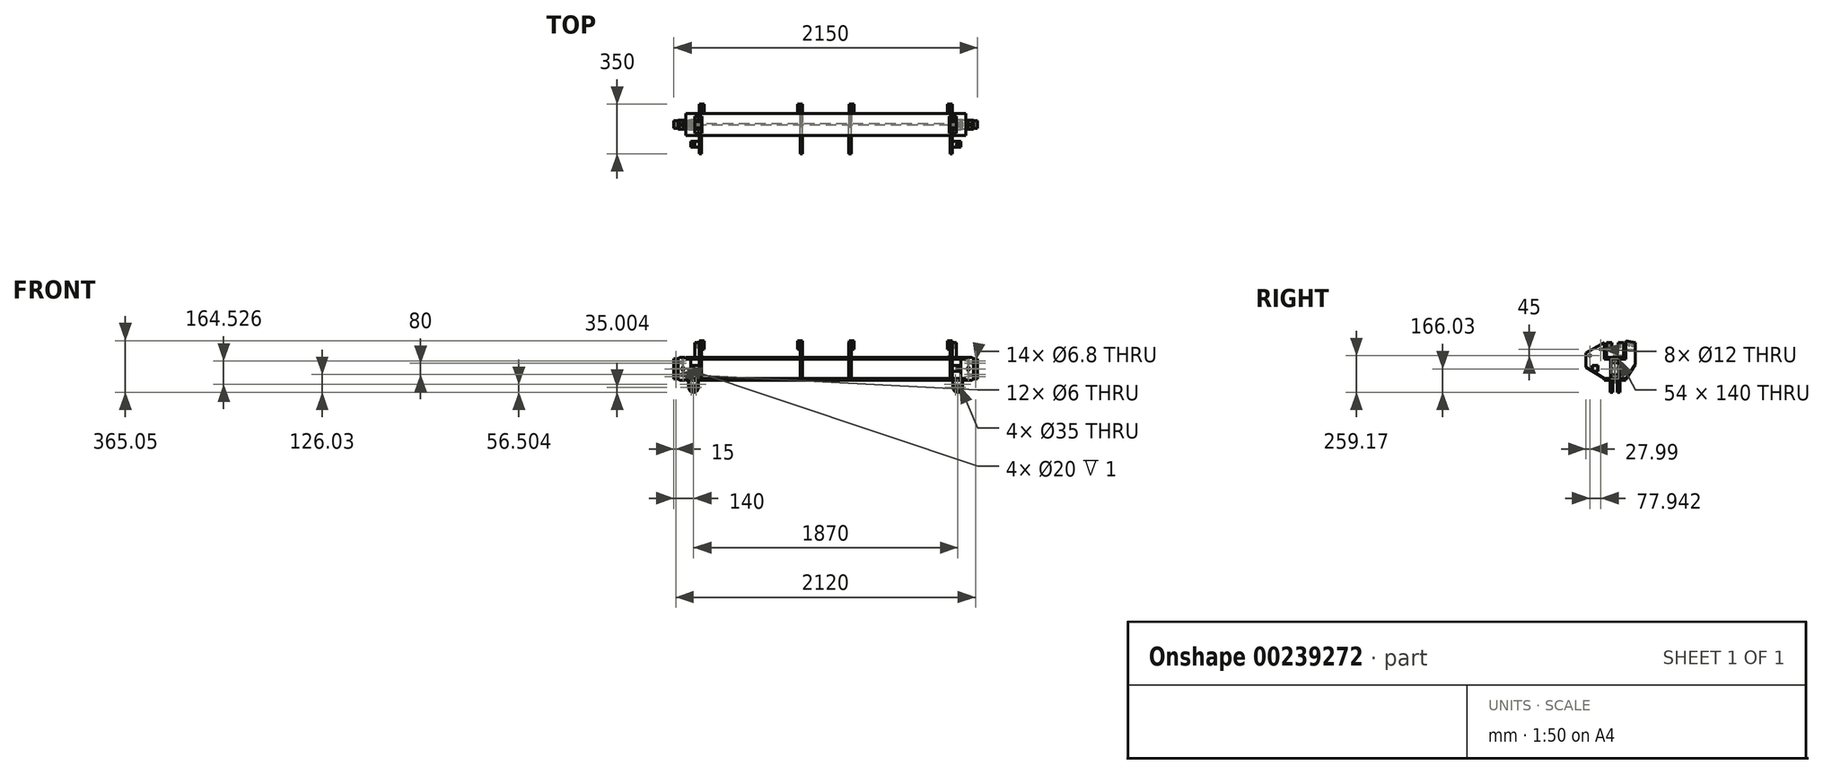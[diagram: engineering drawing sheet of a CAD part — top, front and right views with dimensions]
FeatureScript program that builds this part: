
annotation { "Feature Type Name" : "Feature", "Feature Type Description" : "" }
export const myFeature = defineFeature(function(context is Context, id is Id, definition is map)
    precondition{}
    {
        {
            var Q0;
            Q0=qCreatedBy(makeId("Right.planeOp"),FACE);
            var sketch = newSketch(context, id + "F0", { "sketchPlane" : qUnion([Q0])});
            skLineSegment(sketch, "E0.bottom", {"start": v(-77.22, 81.03) * mm, "end": v(77.22, 81.03) * mm});
            skLineSegment(sketch, "E0.top", {"start": v(-77.22, -81.03) * mm, "end": v(77.22, -81.03) * mm});
            skLineSegment(sketch, "E0.left", {"start": v(-77.22, 81.03) * mm, "end": v(-77.22, 69.47) * mm});
            skLineSegment(sketch, "E0.right", {"start": v(77.22, 81.03) * mm, "end": v(77.22, 69.47) * mm});
            skPoint(sketch, "E0.middle", {"position": v(0, 0) * mm});
            skLineSegment(sketch, "E1", {"start": v(0, 87.3) * mm, "end": v(0, -92.44) * mm, "construction": true});
            skLineSegment(sketch, "E2.0", {"start": v(-77.22, 69.47) * mm, "end": v(-16.76, 69.47) * mm});
            skLineSegment(sketch, "E3.0", {"start": v(-77.22, -69.47) * mm, "end": v(-16.76, -69.47) * mm});
            skLineSegment(sketch, "E4.0", {"start": v(-4.06, 56.77) * mm, "end": v(-4.06, -56.77) * mm});
            skLineSegment(sketch, "E5.0", {"start": v(4.06, 56.77) * mm, "end": v(4.06, -56.77) * mm});
            skLineSegment(sketch, "E6.trimOffspring", {"start": v(16.76, -69.47) * mm, "end": v(77.22, -69.47) * mm});
            skLineSegment(sketch, "E7.trimOffspring", {"start": v(16.76, 69.47) * mm, "end": v(77.22, 69.47) * mm});
            skLineSegment(sketch, "E8.trimOffspring", {"start": v(-77.22, -69.47) * mm, "end": v(-77.22, -81.03) * mm});
            skLineSegment(sketch, "E9.trimOffspring", {"start": v(77.22, -69.47) * mm, "end": v(77.22, -81.03) * mm});
            skPoint(sketch, "E10.visualSharp", {"position": v(-4.06, 69.47) * mm});
            skArc(sketch, "E10.filletArc", {"start": v(-4.06, 56.77) * mm, "mid": v(-7.78, 65.75) * mm, "end": v(-16.76, 69.47) * mm});
            skPoint(sketch, "E11.visualSharp", {"position": v(4.06, 69.47) * mm});
            skArc(sketch, "E11.filletArc", {"start": v(16.76, 69.47) * mm, "mid": v(7.78, 65.75) * mm, "end": v(4.06, 56.77) * mm});
            skPoint(sketch, "E12.visualSharp", {"position": v(4.06, -69.47) * mm});
            skArc(sketch, "E12.filletArc", {"start": v(4.06, -56.77) * mm, "mid": v(7.78, -65.75) * mm, "end": v(16.76, -69.47) * mm});
            skPoint(sketch, "E13.visualSharp", {"position": v(-4.06, -69.47) * mm});
            skArc(sketch, "E13.filletArc", {"start": v(-16.76, -69.47) * mm, "mid": v(-7.78, -65.75) * mm, "end": v(-4.06, -56.77) * mm});
            skSolve(sketch);
        }
        {
            var Q0;
            Q0 = qSketchRegion(id + "F0", true);
            extrude(context, id + "F1", {"entities" : qUnion([Q0]), "endBound" : BoundingType.SYMMETRIC, "depth" : 1980 * mm});
        }
        {
            var Q0;
            Q0=makeQuery(id+"F1.opExtrude","SWEPT_FACE",FACE,{"disambiguationData":[OSD([sQuery(id+"F0.wireOp",EDGE,"E4.0")])]});
            var sketch = newSketch(context, id + "F2", { "sketchPlane" : qUnion([Q0])});
            skLineSegment(sketch, "E14", {"start": v(0, 173.84) * mm, "end": v(0, -192.2) * mm, "construction": true});
            skLineSegment(sketch, "E15.0", {"start": v(-990, 69.47) * mm, "end": v(-990, -69.47) * mm, "construction": true});
            skLineSegment(sketch, "E16.0", {"start": v(990, 69.47) * mm, "end": v(-990, 69.47) * mm, "construction": true});
            skLineSegment(sketch, "E17.0", {"start": v(990, -69.47) * mm, "end": v(-990, -69.47) * mm, "construction": true});
            skPoint(sketch, "E18.orphan", {"position": v(-990, 56.77) * mm});
            skPoint(sketch, "E19.orphan", {"position": v(-990, -56.77) * mm});
            skLineSegment(sketch, "E20.bottom", {"start": v(-990, 69.47) * mm, "end": v(-955, 69.47) * mm});
            skLineSegment(sketch, "E20.top", {"start": v(-990, -69.47) * mm, "end": v(-955, -69.47) * mm});
            skLineSegment(sketch, "E20.left", {"start": v(-990, 69.47) * mm, "end": v(-990, -69.47) * mm});
            skLineSegment(sketch, "E20.right", {"start": v(-955, 69.47) * mm, "end": v(-955, -69.47) * mm});
            skLineSegment(sketch, "E21.MirrorCS", {"start": v(990, -69.47) * mm, "end": v(955, -69.47) * mm});
            skLineSegment(sketch, "E22.MirrorCS", {"start": v(990, 69.47) * mm, "end": v(955, 69.47) * mm});
            skLineSegment(sketch, "E23.MirrorCS", {"start": v(990, 69.47) * mm, "end": v(990, -69.47) * mm});
            skLineSegment(sketch, "E24.MirrorCS", {"start": v(955, 69.47) * mm, "end": v(955, -69.47) * mm});
            skPoint(sketch, "E25.MirrorP", {"position": v(990, -56.77) * mm});
            skPoint(sketch, "E26.MirrorP", {"position": v(990, 56.77) * mm});
            skLineSegment(sketch, "E27.MirrorCS", {"start": v(990, 69.47) * mm, "end": v(990, -69.47) * mm, "construction": true});
            skSolve(sketch);
        }
        {
            var Q0;
            Q0 = qSketchRegion(id + "F2", true);
            extrude(context, id + "F3", {"entities" : qUnion([Q0]), "operationType" : NewBodyOperationType.REMOVE, "endBound" : BoundingType.SYMMETRIC, "oppositeDirection" : true, "depth" : 50 * mm});
        }
        {
            var Q0;
            Q0=qCreatedBy(makeId("Front.planeOp"),FACE);
            var sketch = newSketch(context, id + "F4", { "sketchPlane" : qUnion([Q0])});
            skLineSegment(sketch, "E28", {"start": v(0, 276.7) * mm, "end": v(0, -349.05) * mm, "construction": true});
            skLineSegment(sketch, "E29.0", {"start": v(-1075, 276.7) * mm, "end": v(-1075, -349.05) * mm, "construction": true});
            skLineSegment(sketch, "E30.0", {"start": v(990, 81.03) * mm, "end": v(-1045, 81.03) * mm, "construction": true});
            skLineSegment(sketch, "E31.0", {"start": v(990, -81.03) * mm, "end": v(-1045, -81.03) * mm, "construction": true});
            skLineSegment(sketch, "E32.0", {"start": v(-955, -69.47) * mm, "end": v(-955, 69.47) * mm, "construction": true});
            skLineSegment(sketch, "E33.0", {"start": v(990, -69.47) * mm, "end": v(-990, -69.47) * mm, "construction": true});
            skLineSegment(sketch, "E34.0", {"start": v(990, 69.47) * mm, "end": v(-990, 69.47) * mm, "construction": true});
            skPoint(sketch, "E35.orphan", {"position": v(-955, 56.77) * mm});
            skPoint(sketch, "E36.orphan", {"position": v(-955, -56.77) * mm});
            skPoint(sketch, "E37.orphan", {"position": v(-990, 81.03) * mm});
            skPoint(sketch, "E38.orphan", {"position": v(-990, -81.03) * mm});
            skLineSegment(sketch, "E39", {"start": v(-990, 81.03) * mm, "end": v(-990, 69.47) * mm, "construction": true});
            skLineSegment(sketch, "E40.0", {"start": v(-1045, 81.03) * mm, "end": v(-1045, 70) * mm, "construction": true});
            skLineSegment(sketch, "E41", {"start": v(0, 0) * mm, "end": v(-1199.42, 0) * mm, "construction": true});
            skLineSegment(sketch, "E42.0", {"start": v(0, 70) * mm, "end": v(-990, 70) * mm, "construction": true});
            skLineSegment(sketch, "E43.trimOffspring", {"start": v(-1045, 70) * mm, "end": v(-1075, 70) * mm, "construction": true});
            skLineSegment(sketch, "E44.MirrorCS", {"start": v(-1045, -70) * mm, "end": v(-1075, -70) * mm, "construction": true});
            skPoint(sketch, "E45.orphan", {"position": v(-1199.42, 70) * mm});
            skPoint(sketch, "E46.orphan", {"position": v(-1199.42, -70) * mm});
            skLineSegment(sketch, "E47.trimOffspring", {"start": v(-1045, -70) * mm, "end": v(-1045, -81.03) * mm, "construction": true});
            skLineSegment(sketch, "E48.trimOffspring", {"start": v(-990, -69.47) * mm, "end": v(-990, -81.03) * mm, "construction": true});
            skLineSegment(sketch, "E49.bottom", {"start": v(-1075, 70) * mm, "end": v(-1045, 70) * mm});
            skLineSegment(sketch, "E49.top", {"start": v(-1075, -70) * mm, "end": v(-1045, -70) * mm});
            skLineSegment(sketch, "E49.left", {"start": v(-1075, 70) * mm, "end": v(-1075, -70) * mm});
            skLineSegment(sketch, "E50.bottom", {"start": v(-1045, 81.03) * mm, "end": v(-990, 81.03) * mm});
            skLineSegment(sketch, "E50.top", {"start": v(-1045, -81.03) * mm, "end": v(-990, -81.03) * mm});
            skLineSegment(sketch, "E50.left", {"start": v(-1045, 81.03) * mm, "end": v(-1045, 70) * mm});
            skLineSegment(sketch, "E50.right", {"start": v(-990, 81.03) * mm, "end": v(-990, 69.47) * mm});
            skLineSegment(sketch, "E51.bottom", {"start": v(-990, 70) * mm, "end": v(-955, 70) * mm});
            skLineSegment(sketch, "E51.top", {"start": v(-990, -69.47) * mm, "end": v(-955, -69.47) * mm});
            skLineSegment(sketch, "E51.left", {"start": v(-990, 70) * mm, "end": v(-990, 69.47) * mm});
            skLineSegment(sketch, "E51.right", {"start": v(-955, 70) * mm, "end": v(-955, -69.47) * mm});
            skLineSegment(sketch, "E52.trimOffspring", {"start": v(-990, -69.47) * mm, "end": v(-990, -81.03) * mm});
            skLineSegment(sketch, "E53.trimOffspring", {"start": v(-1045, -70) * mm, "end": v(-1045, -81.03) * mm});
            skSolve(sketch);
        }
        {
            var Q0;
            Q0 = qSketchRegion(id + "F4", true);
            extrude(context, id + "F5", {"entities" : qUnion([Q0]), "endBound" : BoundingType.SYMMETRIC, "depth" : 63.5 * mm});
        }
        {
            var Q0;
            Q0=makeQuery(id+"F5.opExtrude","SWEPT_FACE",FACE,{"disambiguationData":[OSD([sQuery(id+"F4.wireOp",EDGE,"E49.bottom")])]});
            var sketch = newSketch(context, id + "F6", { "sketchPlane" : qUnion([Q0])});
            skLineSegment(sketch, "E54", {"start": v(-948.4, 0) * mm, "end": v(-1101.52, 0) * mm, "construction": true});
            skLineSegment(sketch, "E55.0", {"start": v(-1045, -31.75) * mm, "end": v(-1045, 31.75) * mm, "construction": true});
            skLineSegment(sketch, "E56.0", {"start": v(-948.4, 27) * mm, "end": v(-1101.52, 27) * mm, "construction": true});
            skLineSegment(sketch, "E57.bottom", {"start": v(-1075, 31.75) * mm, "end": v(-1045, 31.75) * mm});
            skLineSegment(sketch, "E57.top", {"start": v(-1075, 27) * mm, "end": v(-1045, 27) * mm});
            skLineSegment(sketch, "E57.left", {"start": v(-1075, 31.75) * mm, "end": v(-1075, 27) * mm});
            skLineSegment(sketch, "E57.right", {"start": v(-1045, 31.75) * mm, "end": v(-1045, 27) * mm});
            skLineSegment(sketch, "E58.MirrorCS", {"start": v(-1045, -31.75) * mm, "end": v(-1045, -27) * mm});
            skLineSegment(sketch, "E59.MirrorCS", {"start": v(-1075, -31.75) * mm, "end": v(-1075, -27) * mm});
            skLineSegment(sketch, "E60.MirrorCS", {"start": v(-1075, -27) * mm, "end": v(-1045, -27) * mm});
            skLineSegment(sketch, "E61.MirrorCS", {"start": v(-1075, -31.75) * mm, "end": v(-1045, -31.75) * mm});
            skSolve(sketch);
        }
        {
            var Q0;
            Q0 = qSketchRegion(id + "F6", true);
            extrude(context, id + "F7", {"entities" : qUnion([Q0]), "operationType" : NewBodyOperationType.REMOVE, "endBound" : BoundingType.THROUGH_ALL, "oppositeDirection" : true, "depth" : 25 * mm});
        }
        {
            var Q0;
            Q0=makeQuery(id+"F5.opExtrude","SWEPT_FACE",FACE,{"disambiguationData":[OSD([sQuery(id+"F4.wireOp",EDGE,"E50.bottom")])]});
            var sketch = newSketch(context, id + "F8", { "sketchPlane" : qUnion([Q0])});
            skLineSegment(sketch, "E62.0", {"start": v(-1075, -27) * mm, "end": v(-1075, 27) * mm, "construction": true});
            skLineSegment(sketch, "E63", {"start": v(-919.6, 0) * mm, "end": v(-1088.25, 0) * mm, "construction": true});
            skPoint(sketch, "E63.endSnap0", {"position": v(-1075, 0) * mm});
            skLineSegment(sketch, "E64.0", {"start": v(-1010, -27) * mm, "end": v(-1010, 27) * mm, "construction": true});
            skPoint(sketch, "E65", {"position": v(-1010, 0) * mm});
            skSolve(sketch);
        }
        {
            var Q0;
            Q0=sQuery(id+"F8.wireOp",VERTEX,"E65");
            var Q1;
            Q1=makeQuery(id+"F5.opExtrude","SWEPT_BODY",BODY,{"disambiguationData":[OSD([sQuery(id+"F4.wireOp",EDGE,"E49.bottom"),sQuery(id+"F4.wireOp",EDGE,"E49.top"),sQuery(id+"F4.wireOp",EDGE,"E49.left"),sQuery(id+"F4.wireOp",EDGE,"E50.bottom"),sQuery(id+"F4.wireOp",EDGE,"E50.top"),sQuery(id+"F4.wireOp",EDGE,"E50.left"),sQuery(id+"F4.wireOp",EDGE,"E50.right"),sQuery(id+"F4.wireOp",EDGE,"E51.bottom"),sQuery(id+"F4.wireOp",EDGE,"E51.top"),sQuery(id+"F4.wireOp",EDGE,"E51.right"),sQuery(id+"F4.wireOp",EDGE,"E52.trimOffspring"),sQuery(id+"F4.wireOp",EDGE,"E53.trimOffspring")])]});
            hole(context, id + "F9", {"style" : HoleStyle.SIMPLE, "endStyle" : HoleEndStyle.BLIND, "standardTappedOrClearance" : lookupTablePath({ "standard" : "ISO", "size" : "6", "type" : "Drilled" }), "standardBlindInLast" : lookupTablePath({ "standard" : "ISO", "size" : "6", "type" : "Drilled" }), "holeDiameter" : 6 * mm, "holeDepth" : 125 * mm, "locations" : qUnion([Q0]), "scope" : qUnion([Q1])});
        }
        {
            var Q0;
            Q0=sQuery(id+"F8.wireOp",VERTEX,"E65");
            var Q1;
            Q1=makeQuery(id+"F5.opExtrude","SWEPT_BODY",BODY,{"disambiguationData":[OSD([sQuery(id+"F4.wireOp",EDGE,"E49.bottom"),sQuery(id+"F4.wireOp",EDGE,"E49.top"),sQuery(id+"F4.wireOp",EDGE,"E49.left"),sQuery(id+"F4.wireOp",EDGE,"E50.bottom"),sQuery(id+"F4.wireOp",EDGE,"E50.top"),sQuery(id+"F4.wireOp",EDGE,"E50.left"),sQuery(id+"F4.wireOp",EDGE,"E50.right"),sQuery(id+"F4.wireOp",EDGE,"E51.bottom"),sQuery(id+"F4.wireOp",EDGE,"E51.top"),sQuery(id+"F4.wireOp",EDGE,"E51.right"),sQuery(id+"F4.wireOp",EDGE,"E52.trimOffspring"),sQuery(id+"F4.wireOp",EDGE,"E53.trimOffspring")])]});
            hole(context, id + "F10", {"style" : HoleStyle.SIMPLE, "endStyle" : HoleEndStyle.BLIND, "standardTappedOrClearance" : lookupTablePath({ "standard" : "ANSI", "engagement" : "75%", "pitch" : "13 tpi", "size" : "1/2", "type" : "Tapped" }), "standardBlindInLast" : lookupTablePath({ "standard" : "ANSI", "engagement" : "75%", "pitch" : "13 tpi", "size" : "1/2", "type" : "Tapped" }), "holeDiameter" : 10.72 * mm, "holeDepth" : 15 * mm, "locations" : qUnion([Q0]), "scope" : qUnion([Q1]), "majorDiameter" : 12.7 * mm});
        }
        {
            var Q0;
            {var subQ0=sQuery(id+"F4.wireOp",EDGE,"E50.bottom");Q0=makeQuery(id+"F8.imprint","IMPRINT",FACE,{"disambiguationData":[TD([[makeQuery(id+"F8.imprint","IMPRINT",EDGE,{"derivedFrom":makeQuery(id+"F5.opExtrude","CAP_EDGE",EDGE,{"disambiguationData":[OSD([subQ0])],"isStart":true})}),-1.0]])]});}
            var sketch = newSketch(context, id + "F11", { "sketchPlane" : qUnion([Q0])});
            skPoint(sketch, "E66.0", {"position": v(-1010, 0) * mm});
            skCircle(sketch, "E67", {"center": v(-1010, 0) * mm, "radius": 10 * mm});
            skSolve(sketch);
        }
        {
            var Q0;
            Q0 = qSketchRegion(id + "F11", true);
            extrude(context, id + "F12", {"entities" : qUnion([Q0]), "operationType" : NewBodyOperationType.REMOVE, "oppositeDirection" : true, "depth" : 1 * mm});
        }
        {
            var Q0;
            Q0=makeQuery(id+"F5.opExtrude","SWEPT_EDGE",EDGE,{"disambiguationData":[OSD([sQuery(id+"F4.wireOp",EDGE,"E50.bottom"),sQuery(id+"F4.wireOp",EDGE,"E50.left")])]});
            var Q1;
            Q1=makeQuery(id+"F7.boolean.opBoolean","INTERSECT",EDGE,{"derivedFrom":[makeQuery(id+"F7.opExtrude","SWEPT_FACE",FACE,{"disambiguationData":[OSD([sQuery(id+"F6.wireOp",EDGE,"E57.right")])]}),makeQuery(id+"F7.opExtrude","SWEPT_FACE",FACE,{"disambiguationData":[OSD([sQuery(id+"F6.wireOp",EDGE,"E58.MirrorCS")])]})]});
            chamfer(context, id + "F13", {"entities" : qUnion([Q0, Q1]), "width" : 11 * mm, "tangentPropagation" : true});
        }
        {
            var Q0;
            Q0=makeQuery(id+"F5.opExtrude","CAP_FACE",FACE,{"disambiguationData":[OSD([sQuery(id+"F4.wireOp",EDGE,"E49.bottom"),sQuery(id+"F4.wireOp",EDGE,"E49.top"),sQuery(id+"F4.wireOp",EDGE,"E49.left"),sQuery(id+"F4.wireOp",EDGE,"E50.bottom"),sQuery(id+"F4.wireOp",EDGE,"E50.top"),sQuery(id+"F4.wireOp",EDGE,"E50.left"),sQuery(id+"F4.wireOp",EDGE,"E50.right"),sQuery(id+"F4.wireOp",EDGE,"E51.bottom"),sQuery(id+"F4.wireOp",EDGE,"E51.top"),sQuery(id+"F4.wireOp",EDGE,"E51.right"),sQuery(id+"F4.wireOp",EDGE,"E52.trimOffspring"),sQuery(id+"F4.wireOp",EDGE,"E53.trimOffspring")])],"isStart":false});
            var sketch = newSketch(context, id + "F14", { "sketchPlane" : qUnion([Q0])});
            skLineSegment(sketch, "E68", {"start": v(-947.26, 0.27) * mm, "end": v(-1104.17, 0.27) * mm, "construction": true});
            skPoint(sketch, "E68.startSnap0", {"position": v(-955, 0.27) * mm});
            skLineSegment(sketch, "E69.0", {"start": v(-1075, -70) * mm, "end": v(-1075, 70) * mm, "construction": true});
            skLineSegment(sketch, "E70.0", {"start": v(-1010, -70) * mm, "end": v(-1010, 70) * mm, "construction": true});
            skPoint(sketch, "E71", {"position": v(-1010, 0.27) * mm});
            skSolve(sketch);
        }
        {
            var Q0;
            Q0=sQuery(id+"F14.wireOp",VERTEX,"E71");
            var Q1;
            Q1=makeQuery(id+"F5.opExtrude","SWEPT_BODY",BODY,{"disambiguationData":[OSD([sQuery(id+"F4.wireOp",EDGE,"E49.bottom"),sQuery(id+"F4.wireOp",EDGE,"E49.top"),sQuery(id+"F4.wireOp",EDGE,"E49.left"),sQuery(id+"F4.wireOp",EDGE,"E50.bottom"),sQuery(id+"F4.wireOp",EDGE,"E50.top"),sQuery(id+"F4.wireOp",EDGE,"E50.left"),sQuery(id+"F4.wireOp",EDGE,"E50.right"),sQuery(id+"F4.wireOp",EDGE,"E51.bottom"),sQuery(id+"F4.wireOp",EDGE,"E51.top"),sQuery(id+"F4.wireOp",EDGE,"E51.right"),sQuery(id+"F4.wireOp",EDGE,"E52.trimOffspring"),sQuery(id+"F4.wireOp",EDGE,"E53.trimOffspring")])]});
            hole(context, id + "F15", {"style" : HoleStyle.SIMPLE, "endStyle" : HoleEndStyle.BLIND, "standardTappedOrClearance" : lookupTablePath({ "standard" : "ANSI", "engagement" : "75%", "pitch" : "13 tpi", "size" : "1/2", "type" : "Tapped" }), "standardBlindInLast" : lookupTablePath({ "standard" : "ANSI", "engagement" : "75%", "pitch" : "13 tpi", "size" : "1/2", "type" : "Tapped" }), "holeDiameter" : 10.72 * mm, "holeDepth" : 15 * mm, "locations" : qUnion([Q0]), "scope" : qUnion([Q1]), "majorDiameter" : 12.7 * mm});
        }
        {
            var Q0;
            Q0=sQuery(id+"F14.wireOp",VERTEX,"E71");
            var Q1;
            Q1=makeQuery(id+"F5.opExtrude","SWEPT_BODY",BODY,{"disambiguationData":[OSD([sQuery(id+"F4.wireOp",EDGE,"E49.bottom"),sQuery(id+"F4.wireOp",EDGE,"E49.top"),sQuery(id+"F4.wireOp",EDGE,"E49.left"),sQuery(id+"F4.wireOp",EDGE,"E50.bottom"),sQuery(id+"F4.wireOp",EDGE,"E50.top"),sQuery(id+"F4.wireOp",EDGE,"E50.left"),sQuery(id+"F4.wireOp",EDGE,"E50.right"),sQuery(id+"F4.wireOp",EDGE,"E51.bottom"),sQuery(id+"F4.wireOp",EDGE,"E51.top"),sQuery(id+"F4.wireOp",EDGE,"E51.right"),sQuery(id+"F4.wireOp",EDGE,"E52.trimOffspring"),sQuery(id+"F4.wireOp",EDGE,"E53.trimOffspring")])]});
            hole(context, id + "F16", {"style" : HoleStyle.SIMPLE, "endStyle" : HoleEndStyle.THROUGH, "standardTappedOrClearance" : lookupTablePath({ "standard" : "ISO", "size" : "6", "type" : "Drilled" }), "standardBlindInLast" : lookupTablePath({ "standard" : "ISO", "size" : "6", "type" : "Drilled" }), "holeDiameter" : 6 * mm, "locations" : qUnion([Q0]), "scope" : qUnion([Q1]), "isTappedThrough" : true});
        }
        {
            var Q0;
            {var subQ4=sQuery(id+"F4.wireOp",EDGE,"E50.right");Q0=makeQuery(id+"F14.imprint","IMPRINT",FACE,{"disambiguationData":[TD([[makeQuery(id+"F14.imprint","IMPRINT",EDGE,{"derivedFrom":makeQuery(id+"F5.opExtrude","CAP_EDGE",EDGE,{"disambiguationData":[OSD([subQ4])],"isStart":false})}),-1.0]])]});}
            var sketch = newSketch(context, id + "F17", { "sketchPlane" : qUnion([Q0])});
            skCircle(sketch, "E72", {"center": v(-1010, 0.27) * mm, "radius": 10 * mm});
            skSolve(sketch);
        }
        {
            var Q0;
            Q0 = qSketchRegion(id + "F17", true);
            extrude(context, id + "F18", {"entities" : qUnion([Q0]), "operationType" : NewBodyOperationType.REMOVE, "oppositeDirection" : true, "depth" : 1 * mm});
        }
        {
            var Q0;
            Q0=makeQuery(id+"F5.opExtrude","CAP_FACE",FACE,{"disambiguationData":[OSD([sQuery(id+"F4.wireOp",EDGE,"E49.bottom"),sQuery(id+"F4.wireOp",EDGE,"E49.top"),sQuery(id+"F4.wireOp",EDGE,"E49.left"),sQuery(id+"F4.wireOp",EDGE,"E50.bottom"),sQuery(id+"F4.wireOp",EDGE,"E50.top"),sQuery(id+"F4.wireOp",EDGE,"E50.left"),sQuery(id+"F4.wireOp",EDGE,"E50.right"),sQuery(id+"F4.wireOp",EDGE,"E51.bottom"),sQuery(id+"F4.wireOp",EDGE,"E51.top"),sQuery(id+"F4.wireOp",EDGE,"E51.right"),sQuery(id+"F4.wireOp",EDGE,"E52.trimOffspring"),sQuery(id+"F4.wireOp",EDGE,"E53.trimOffspring")])],"isStart":true});
            var sketch = newSketch(context, id + "F19", { "sketchPlane" : qUnion([Q0])});
            skCircle(sketch, "E73.0", {"center": v(1010, 0.27) * mm, "radius": 10 * mm, "construction": true});
            skCircle(sketch, "E74", {"center": v(1010, 0.27) * mm, "radius": 10 * mm});
            skSolve(sketch);
        }
        {
            var Q0;
            Q0 = qSketchRegion(id + "F19", true);
            extrude(context, id + "F20", {"entities" : qUnion([Q0]), "operationType" : NewBodyOperationType.REMOVE, "oppositeDirection" : true, "depth" : 1 * mm});
        }
        {
            var Q0;
            Q0=sQuery(id+"F19.wireOp",VERTEX,"E73.0.center");
            var Q1;
            Q1=makeQuery(id+"F5.opExtrude","SWEPT_BODY",BODY,{"disambiguationData":[OSD([sQuery(id+"F4.wireOp",EDGE,"E49.bottom"),sQuery(id+"F4.wireOp",EDGE,"E49.top"),sQuery(id+"F4.wireOp",EDGE,"E49.left"),sQuery(id+"F4.wireOp",EDGE,"E50.bottom"),sQuery(id+"F4.wireOp",EDGE,"E50.top"),sQuery(id+"F4.wireOp",EDGE,"E50.left"),sQuery(id+"F4.wireOp",EDGE,"E50.right"),sQuery(id+"F4.wireOp",EDGE,"E51.bottom"),sQuery(id+"F4.wireOp",EDGE,"E51.top"),sQuery(id+"F4.wireOp",EDGE,"E51.right"),sQuery(id+"F4.wireOp",EDGE,"E52.trimOffspring"),sQuery(id+"F4.wireOp",EDGE,"E53.trimOffspring")])]});
            hole(context, id + "F21", {"style" : HoleStyle.SIMPLE, "endStyle" : HoleEndStyle.BLIND, "standardTappedOrClearance" : lookupTablePath({ "standard" : "ANSI", "engagement" : "75%", "pitch" : "13 tpi", "size" : "1/2", "type" : "Tapped" }), "standardBlindInLast" : lookupTablePath({ "standard" : "ANSI", "engagement" : "75%", "pitch" : "13 tpi", "size" : "1/2", "type" : "Tapped" }), "holeDiameter" : 10.72 * mm, "holeDepth" : 15 * mm, "locations" : qUnion([Q0]), "scope" : qUnion([Q1]), "majorDiameter" : 12.7 * mm});
        }
        {
            var Q0;
            Q0=makeQuery(id+"F7.boolean.opBoolean","COPY",FACE,{"derivedFrom":makeQuery(id+"F7.opExtrude","SWEPT_FACE",FACE,{"disambiguationData":[OSD([sQuery(id+"F6.wireOp",EDGE,"E60.MirrorCS")])]})});
            var sketch = newSketch(context, id + "F22", { "sketchPlane" : qUnion([Q0])});
            skLineSegment(sketch, "E75.0", {"start": v(-1075, -70) * mm, "end": v(-1075, 70) * mm, "construction": true});
            skLineSegment(sketch, "E76.0", {"start": v(-1060, -70) * mm, "end": v(-1060, 70) * mm, "construction": true});
            skLineSegment(sketch, "E77", {"start": v(-1060, 0) * mm, "end": v(-1136.9, 0) * mm, "construction": true});
            skLineSegment(sketch, "E78.0", {"start": v(-1060, 55) * mm, "end": v(-1136.9, 55) * mm, "construction": true});
            skLineSegment(sketch, "E79.0", {"start": v(-1060, -55) * mm, "end": v(-1136.9, -55) * mm, "construction": true});
            skPoint(sketch, "E80", {"position": v(-1060, 55) * mm});
            skPoint(sketch, "E81", {"position": v(-1060, 0) * mm});
            skPoint(sketch, "E82", {"position": v(-1060, -55) * mm});
            skSolve(sketch);
        }
        {
            var Q0;
            Q0=sQuery(id+"F22.wireOp",VERTEX,"E80");
            var Q1;
            Q1=sQuery(id+"F22.wireOp",VERTEX,"E81");
            var Q2;
            Q2=sQuery(id+"F22.wireOp",VERTEX,"E82");
            var Q3;
            Q3=makeQuery(id+"F5.opExtrude","SWEPT_BODY",BODY,{"disambiguationData":[OSD([sQuery(id+"F4.wireOp",EDGE,"E49.bottom"),sQuery(id+"F4.wireOp",EDGE,"E49.top"),sQuery(id+"F4.wireOp",EDGE,"E49.left"),sQuery(id+"F4.wireOp",EDGE,"E50.bottom"),sQuery(id+"F4.wireOp",EDGE,"E50.top"),sQuery(id+"F4.wireOp",EDGE,"E50.left"),sQuery(id+"F4.wireOp",EDGE,"E50.right"),sQuery(id+"F4.wireOp",EDGE,"E51.bottom"),sQuery(id+"F4.wireOp",EDGE,"E51.top"),sQuery(id+"F4.wireOp",EDGE,"E51.right"),sQuery(id+"F4.wireOp",EDGE,"E52.trimOffspring"),sQuery(id+"F4.wireOp",EDGE,"E53.trimOffspring")])]});
            hole(context, id + "F23", {"style" : HoleStyle.SIMPLE, "endStyle" : HoleEndStyle.THROUGH, "standardTappedOrClearance" : lookupTablePath({ "standard" : "ISO", "engagement" : "75%", "pitch" : "1.25 mm", "size" : "M8", "type" : "Tapped" }), "standardBlindInLast" : lookupTablePath({ "standard" : "ISO", "engagement" : "75%", "pitch" : "1.25 mm", "size" : "M8", "type" : "Tapped" }), "holeDiameter" : 6.8 * mm, "locations" : qUnion([Q0, Q1, Q2]), "scope" : qUnion([Q3]), "isTappedThrough" : true, "majorDiameter" : 8 * mm, "showTappedDepth" : true});
        }
        {
            var Q0;
            Q0=makeQuery(id+"F7.boolean.opBoolean","COPY",FACE,{"derivedFrom":makeQuery(id+"F7.opExtrude","SWEPT_FACE",FACE,{"disambiguationData":[OSD([sQuery(id+"F6.wireOp",EDGE,"E60.MirrorCS")])]})});
            var sketch = newSketch(context, id + "F24", { "sketchPlane" : qUnion([Q0])});
            skLineSegment(sketch, "E83.0", {"start": v(-1060, 0) * mm, "end": v(-1136.9, 0) * mm, "construction": true});
            skLineSegment(sketch, "E84.0", {"start": v(-1060, -70) * mm, "end": v(-1060, 70) * mm, "construction": true});
            skLineSegment(sketch, "E85.0", {"start": v(-1060, 40) * mm, "end": v(-1136.9, 40) * mm, "construction": true});
            skPoint(sketch, "E86", {"position": v(-1060, 40) * mm});
            skPoint(sketch, "E87.MirrorP", {"position": v(-1060, -40) * mm});
            skSolve(sketch);
        }
        {
            var Q0;
            Q0=sQuery(id+"F24.wireOp",VERTEX,"E86");
            var Q1;
            Q1=sQuery(id+"F24.wireOp",VERTEX,"E87.MirrorP");
            var Q2;
            Q2=makeQuery(id+"F5.opExtrude","SWEPT_BODY",BODY,{"disambiguationData":[OSD([sQuery(id+"F4.wireOp",EDGE,"E49.bottom"),sQuery(id+"F4.wireOp",EDGE,"E49.top"),sQuery(id+"F4.wireOp",EDGE,"E49.left"),sQuery(id+"F4.wireOp",EDGE,"E50.bottom"),sQuery(id+"F4.wireOp",EDGE,"E50.top"),sQuery(id+"F4.wireOp",EDGE,"E50.left"),sQuery(id+"F4.wireOp",EDGE,"E50.right"),sQuery(id+"F4.wireOp",EDGE,"E51.bottom"),sQuery(id+"F4.wireOp",EDGE,"E51.top"),sQuery(id+"F4.wireOp",EDGE,"E51.right"),sQuery(id+"F4.wireOp",EDGE,"E52.trimOffspring"),sQuery(id+"F4.wireOp",EDGE,"E53.trimOffspring")])]});
            hole(context, id + "F25", {"style" : HoleStyle.SIMPLE, "endStyle" : HoleEndStyle.THROUGH, "standardTappedOrClearance" : lookupTablePath({ "standard" : "ISO", "size" : "6", "type" : "Drilled" }), "standardBlindInLast" : lookupTablePath({ "standard" : "ISO", "size" : "6", "type" : "Drilled" }), "holeDiameter" : 6 * mm, "locations" : qUnion([Q0, Q1]), "scope" : qUnion([Q2]), "isTappedThrough" : true});
        }
        {
            var Q0;
            Q0=makeQuery(id+"F5.opExtrude","SWEPT_FACE",FACE,{"disambiguationData":[OSD([sQuery(id+"F4.wireOp",EDGE,"E49.left")])]});
            var sketch = newSketch(context, id + "F26", { "sketchPlane" : qUnion([Q0])});
            skLineSegment(sketch, "E88.0.0", {"start": v(-27, -70) * mm, "end": v(27, -70) * mm, "construction": true});
            skLineSegment(sketch, "E88.0.1", {"start": v(27, -70) * mm, "end": v(27, 70) * mm, "construction": true});
            skLineSegment(sketch, "E88.0.2", {"start": v(27, 70) * mm, "end": v(-27, 70) * mm, "construction": true});
            skLineSegment(sketch, "E88.0.3", {"start": v(-27, 70) * mm, "end": v(-27, -70) * mm, "construction": true});
            skLineSegment(sketch, "E89", {"start": v(-27, 0) * mm, "end": v(56.48, 0) * mm, "construction": true});
            skPoint(sketch, "E89.endSnap0", {"position": v(-27, 0) * mm});
            skLineSegment(sketch, "E90", {"start": v(0, 96.87) * mm, "end": v(0, -94.28) * mm, "construction": true});
            skLineSegment(sketch, "E91.0", {"start": v(-27, -40) * mm, "end": v(56.48, -40) * mm, "construction": true});
            skPoint(sketch, "E92", {"position": v(0, -40) * mm});
            skPoint(sketch, "E93.MirrorP", {"position": v(0, 40) * mm});
            skSolve(sketch);
        }
        {
            var Q0;
            Q0=sQuery(id+"F26.wireOp",VERTEX,"E93.MirrorP");
            var Q1;
            Q1=sQuery(id+"F26.wireOp",VERTEX,"E92");
            var Q2;
            Q2=makeQuery(id+"F5.opExtrude","SWEPT_BODY",BODY,{"disambiguationData":[OSD([sQuery(id+"F4.wireOp",EDGE,"E49.bottom"),sQuery(id+"F4.wireOp",EDGE,"E49.top"),sQuery(id+"F4.wireOp",EDGE,"E49.left"),sQuery(id+"F4.wireOp",EDGE,"E50.bottom"),sQuery(id+"F4.wireOp",EDGE,"E50.top"),sQuery(id+"F4.wireOp",EDGE,"E50.left"),sQuery(id+"F4.wireOp",EDGE,"E50.right"),sQuery(id+"F4.wireOp",EDGE,"E51.bottom"),sQuery(id+"F4.wireOp",EDGE,"E51.top"),sQuery(id+"F4.wireOp",EDGE,"E51.right"),sQuery(id+"F4.wireOp",EDGE,"E52.trimOffspring"),sQuery(id+"F4.wireOp",EDGE,"E53.trimOffspring")])]});
            hole(context, id + "F27", {"style" : HoleStyle.SIMPLE, "endStyle" : HoleEndStyle.BLIND, "standardTappedOrClearance" : lookupTablePath({ "standard" : "ISO", "size" : "6", "type" : "Drilled" }), "standardBlindInLast" : lookupTablePath({ "standard" : "ISO", "size" : "6", "type" : "Drilled" }), "holeDiameter" : 6 * mm, "holeDepth" : 65 * mm, "locations" : qUnion([Q0, Q1]), "scope" : qUnion([Q2])});
        }
        {
            var Q0;
            Q0=sQuery(id+"F26.wireOp",VERTEX,"E93.MirrorP");
            var Q1;
            Q1=sQuery(id+"F26.wireOp",VERTEX,"E92");
            var Q2;
            Q2=makeQuery(id+"F5.opExtrude","SWEPT_BODY",BODY,{"disambiguationData":[OSD([sQuery(id+"F4.wireOp",EDGE,"E49.bottom"),sQuery(id+"F4.wireOp",EDGE,"E49.top"),sQuery(id+"F4.wireOp",EDGE,"E49.left"),sQuery(id+"F4.wireOp",EDGE,"E50.bottom"),sQuery(id+"F4.wireOp",EDGE,"E50.top"),sQuery(id+"F4.wireOp",EDGE,"E50.left"),sQuery(id+"F4.wireOp",EDGE,"E50.right"),sQuery(id+"F4.wireOp",EDGE,"E51.bottom"),sQuery(id+"F4.wireOp",EDGE,"E51.top"),sQuery(id+"F4.wireOp",EDGE,"E51.right"),sQuery(id+"F4.wireOp",EDGE,"E52.trimOffspring"),sQuery(id+"F4.wireOp",EDGE,"E53.trimOffspring")])]});
            hole(context, id + "F28", {"style" : HoleStyle.SIMPLE, "endStyle" : HoleEndStyle.BLIND, "standardTappedOrClearance" : lookupTablePath({ "standard" : "ISO", "engagement" : "75%", "pitch" : "1.25 mm", "size" : "M8", "type" : "Tapped" }), "standardBlindInLast" : lookupTablePath({ "standard" : "ISO", "engagement" : "75%", "pitch" : "1.25 mm", "size" : "M8", "type" : "Tapped" }), "holeDiameter" : 6.8 * mm, "holeDepth" : 12 * mm, "locations" : qUnion([Q0, Q1]), "scope" : qUnion([Q2]), "majorDiameter" : 8 * mm});
        }
        {
            var Q0;
            Q0=makeQuery(id+"F5.opExtrude","SWEPT_BODY",BODY,{"disambiguationData":[OSD([sQuery(id+"F4.wireOp",EDGE,"E49.bottom"),sQuery(id+"F4.wireOp",EDGE,"E49.top"),sQuery(id+"F4.wireOp",EDGE,"E49.left"),sQuery(id+"F4.wireOp",EDGE,"E50.bottom"),sQuery(id+"F4.wireOp",EDGE,"E50.top"),sQuery(id+"F4.wireOp",EDGE,"E50.left"),sQuery(id+"F4.wireOp",EDGE,"E50.right"),sQuery(id+"F4.wireOp",EDGE,"E51.bottom"),sQuery(id+"F4.wireOp",EDGE,"E51.top"),sQuery(id+"F4.wireOp",EDGE,"E51.right"),sQuery(id+"F4.wireOp",EDGE,"E52.trimOffspring"),sQuery(id+"F4.wireOp",EDGE,"E53.trimOffspring")])]});
            var Q1;
            Q1=qCreatedBy(makeId("Right.planeOp"),FACE);
            mirror(context, id + "F29", {"entities" : qUnion([Q0]), "mirrorPlane" : qUnion([Q1])});
        }
        {
            var Q0;
            Q0=qCreatedBy(makeId("Front.planeOp"),FACE);
            var sketch = newSketch(context, id + "F30", { "sketchPlane" : qUnion([Q0])});
            skLineSegment(sketch, "E94", {"start": v(0, 217.37) * mm, "end": v(0, -483.51) * mm, "construction": true});
            skLineSegment(sketch, "E95.0", {"start": v(-935, 217.37) * mm, "end": v(-935, -483.51) * mm, "construction": true});
            skLineSegment(sketch, "E96.0.0", {"start": v(-990, -69.47) * mm, "end": v(-990, -81.03) * mm, "construction": true});
            skLineSegment(sketch, "E96.0.1", {"start": v(-990, -81.03) * mm, "end": v(-900, -81.03) * mm});
            skLineSegment(sketch, "E96.0.2", {"start": v(990, -81.03) * mm, "end": v(990, -69.47) * mm, "construction": true});
            skLineSegment(sketch, "E96.0.3", {"start": v(990, -69.47) * mm, "end": v(-990, -69.47) * mm, "construction": true});
            skLineSegment(sketch, "E97.0", {"start": v(-990, -131.03) * mm, "end": v(990, -131.03) * mm, "construction": true});
            skCircle(sketch, "E98", {"center": v(-935, -131.03) * mm, "radius": 17.5 * mm});
            skArc(sketch, "E99", {"start": v(-970, -131.03) * mm, "mid": v(-935, -166.03) * mm, "end": v(-900, -131.03) * mm});
            skLineSegment(sketch, "E100", {"start": v(-970, -131.03) * mm, "end": v(-970, -81.03) * mm});
            skLineSegment(sketch, "E101", {"start": v(-900, -131.03) * mm, "end": v(-900, -81.03) * mm});
            skLineSegment(sketch, "E102.trimOffspring", {"start": v(0, -81.03) * mm, "end": v(990, -81.03) * mm});
            skLineSegment(sketch, "E103", {"start": v(-935, -166.03) * mm, "end": v(-989.6, -166.03) * mm, "construction": true});
            skLineSegment(sketch, "E104.0", {"start": v(-935, -144.53) * mm, "end": v(-989.6, -144.53) * mm, "construction": true});
            skLineSegment(sketch, "E105.0", {"start": v(-990, -109.53) * mm, "end": v(990, -109.53) * mm, "construction": true});
            skLineSegment(sketch, "E106.0", {"start": v(-953, 217.37) * mm, "end": v(-953, -483.51) * mm, "construction": true});
            skPoint(sketch, "E107", {"position": v(-953, -109.53) * mm});
            skPoint(sketch, "E108.MirrorP", {"position": v(-917, -109.53) * mm});
            skSolve(sketch);
        }
        {
            var Q0;
            Q0 = qSketchRegion(id + "F30", true);
            extrude(context, id + "F31", {"entities" : qUnion([Q0]), "endBound" : BoundingType.SYMMETRIC, "depth" : 70 * mm});
        }
        {
            var Q0;
            Q0=makeQuery(id+"F31.opExtrude","CAP_FACE",FACE,{"disambiguationData":[OSD([sQuery(id+"F30.wireOp",EDGE,"E96.0.1"),sQuery(id+"F30.wireOp",EDGE,"E98"),sQuery(id+"F30.wireOp",EDGE,"E99"),sQuery(id+"F30.wireOp",EDGE,"E100"),sQuery(id+"F30.wireOp",EDGE,"E101")])],"isStart":false});
            var sketch = newSketch(context, id + "F32", { "sketchPlane" : qUnion([Q0])});
            skPoint(sketch, "E109.0", {"position": v(-953, -109.53) * mm});
            skPoint(sketch, "E110.0", {"position": v(-917, -109.53) * mm});
            skSolve(sketch);
        }
        {
            var Q0;
            Q0=sQuery(id+"F32.wireOp",VERTEX,"E109.0");
            var Q1;
            Q1=sQuery(id+"F32.wireOp",VERTEX,"E110.0");
            var Q2;
            Q2=makeQuery(id+"F31.opExtrude","SWEPT_BODY",BODY,{"disambiguationData":[OSD([sQuery(id+"F30.wireOp",EDGE,"E96.0.1"),sQuery(id+"F30.wireOp",EDGE,"E98"),sQuery(id+"F30.wireOp",EDGE,"E99"),sQuery(id+"F30.wireOp",EDGE,"E100"),sQuery(id+"F30.wireOp",EDGE,"E101")])]});
            hole(context, id + "F33", {"style" : HoleStyle.SIMPLE, "endStyle" : HoleEndStyle.THROUGH, "standardTappedOrClearance" : lookupTablePath({ "standard" : "ISO", "engagement" : "75%", "pitch" : "1.25 mm", "size" : "M8", "type" : "Tapped" }), "standardBlindInLast" : lookupTablePath({ "standard" : "ISO", "engagement" : "75%", "pitch" : "1.25 mm", "size" : "M8", "type" : "Tapped" }), "holeDiameter" : 6.8 * mm, "locations" : qUnion([Q0, Q1]), "scope" : qUnion([Q2]), "isTappedThrough" : true, "majorDiameter" : 8 * mm, "showTappedDepth" : true});
        }
        {
            var Q0;
            Q0=makeQuery(id+"F31.opExtrude","SWEPT_FACE",FACE,{"disambiguationData":[OSD([sQuery(id+"F30.wireOp",EDGE,"E101")])]});
            var sketch = newSketch(context, id + "F34", { "sketchPlane" : qUnion([Q0])});
            skLineSegment(sketch, "E111.0", {"start": v(-35, -81.03) * mm, "end": v(35, -81.03) * mm, "construction": true});
            skLineSegment(sketch, "E112", {"start": v(0, -81.03) * mm, "end": v(0, -181.86) * mm, "construction": true});
            skPoint(sketch, "E112.endSnap0", {"position": v(0, -81.03) * mm});
            skLineSegment(sketch, "E113.0", {"start": v(-15.5, -81.03) * mm, "end": v(-15.5, -181.86) * mm, "construction": true});
            skLineSegment(sketch, "E114", {"start": v(35, -166.03) * mm, "end": v(-35, -166.03) * mm, "construction": true});
            skLineSegment(sketch, "E115.0", {"start": v(35, -148.53) * mm, "end": v(35, -113.53) * mm, "construction": true});
            skLineSegment(sketch, "E116", {"start": v(35, -131.03) * mm, "end": v(-53.23, -131.03) * mm, "construction": true});
            skLineSegment(sketch, "E117.0", {"start": v(35, -87.03) * mm, "end": v(-53.23, -87.03) * mm, "construction": true});
            skLineSegment(sketch, "E118.bottom", {"start": v(-15.5, -166.03) * mm, "end": v(15.5, -166.03) * mm});
            skLineSegment(sketch, "E118.top", {"start": v(-15.5, -87.03) * mm, "end": v(15.5, -87.03) * mm});
            skLineSegment(sketch, "E118.left", {"start": v(-15.5, -166.03) * mm, "end": v(-15.5, -87.03) * mm});
            skLineSegment(sketch, "E118.right", {"start": v(15.5, -166.03) * mm, "end": v(15.5, -87.03) * mm});
            skSolve(sketch);
        }
        {
            var Q0;
            Q0 = qSketchRegion(id + "F34", true);
            extrude(context, id + "F35", {"entities" : qUnion([Q0]), "operationType" : NewBodyOperationType.REMOVE, "endBound" : BoundingType.THROUGH_ALL, "oppositeDirection" : true, "depth" : 25 * mm});
        }
        {
            var Q0;
            Q0=makeQuery(id+"F35.boolean.opBoolean","COPY",EDGE,{"derivedFrom":makeQuery(id+"F35.opExtrude","SWEPT_EDGE",EDGE,{"disambiguationData":[OSD([sQuery(id+"F34.wireOp",EDGE,"E118.top"),sQuery(id+"F34.wireOp",EDGE,"E118.right")])]})});
            var Q1;
            Q1=makeQuery(id+"F35.boolean.opBoolean","COPY",EDGE,{"derivedFrom":makeQuery(id+"F35.opExtrude","SWEPT_EDGE",EDGE,{"disambiguationData":[OSD([sQuery(id+"F34.wireOp",EDGE,"E118.top"),sQuery(id+"F34.wireOp",EDGE,"E118.left")])]})});
            fillet(context, id + "F36", {"entities" : qUnion([Q0, Q1]), "radius" : 2 * mm, "tangentPropagation" : true, "allowEdgeOverflow" : false});
        }
        {
            var Q0;
            Q0=makeQuery(id+"F31.opExtrude","SWEPT_BODY",BODY,{"disambiguationData":[OSD([sQuery(id+"F30.wireOp",EDGE,"E96.0.1"),sQuery(id+"F30.wireOp",EDGE,"E98"),sQuery(id+"F30.wireOp",EDGE,"E99"),sQuery(id+"F30.wireOp",EDGE,"E100"),sQuery(id+"F30.wireOp",EDGE,"E101")])]});
            var Q1;
            Q1=qCreatedBy(makeId("Right.planeOp"),FACE);
            mirror(context, id + "F37", {"entities" : qUnion([Q0]), "mirrorPlane" : qUnion([Q1])});
        }
        {
            var Q0;
            Q0=makeQuery(id+"F1.opExtrude","SWEPT_FACE",FACE,{"disambiguationData":[OSD([sQuery(id+"F0.wireOp",EDGE,"E0.bottom")])]});
            var sketch = newSketch(context, id + "F38", { "sketchPlane" : qUnion([Q0])});
            skLineSegment(sketch, "E119", {"start": v(0, 374.52) * mm, "end": v(0, -390.73) * mm, "construction": true});
            skLineSegment(sketch, "E120.0", {"start": v(-880, 374.52) * mm, "end": v(-880, -390.73) * mm, "construction": true});
            skLineSegment(sketch, "E121.0", {"start": v(-925, 374.52) * mm, "end": v(-925, -390.73) * mm, "construction": true});
            skLineSegment(sketch, "E122.0", {"start": v(-874.2, 374.52) * mm, "end": v(-874.2, -390.73) * mm, "construction": true});
            skPoint(sketch, "E123.endSnap0", {"position": v(0, -8.1) * mm});
            skLineSegment(sketch, "E124.0.0", {"start": v(-990, 77.22) * mm, "end": v(-990, -77.22) * mm, "construction": true});
            skLineSegment(sketch, "E124.0.1", {"start": v(-990, -77.22) * mm, "end": v(990, -77.22) * mm, "construction": true});
            skLineSegment(sketch, "E124.0.2", {"start": v(990, -77.22) * mm, "end": v(990, 77.22) * mm, "construction": true});
            skLineSegment(sketch, "E124.0.3", {"start": v(990, 77.22) * mm, "end": v(-990, 77.22) * mm, "construction": true});
            skLineSegment(sketch, "E125", {"start": v(-990, 0) * mm, "end": v(-602.18, 0) * mm, "construction": true});
            skLineSegment(sketch, "E126.0", {"start": v(-990, 60) * mm, "end": v(-602.18, 60) * mm, "construction": true});
            skLineSegment(sketch, "E127.bottom", {"start": v(-925, 60) * mm, "end": v(-874.2, 60) * mm});
            skLineSegment(sketch, "E127.top", {"start": v(-925, -60) * mm, "end": v(-874.2, -60) * mm});
            skLineSegment(sketch, "E127.left", {"start": v(-925, 60) * mm, "end": v(-925, -60) * mm});
            skLineSegment(sketch, "E127.right", {"start": v(-874.2, 60) * mm, "end": v(-874.2, -60) * mm});
            skSolve(sketch);
        }
        {
            var Q0;
            Q0 = qSketchRegion(id + "F38", true);
            extrude(context, id + "F39", {"entities" : qUnion([Q0]), "depth" : 120 * mm});
        }
        {
            var Q0;
            Q0=makeQuery(id+"F39.opExtrude","SWEPT_FACE",FACE,{"disambiguationData":[OSD([sQuery(id+"F38.wireOp",EDGE,"E127.left")])]});
            var sketch = newSketch(context, id + "F40", { "sketchPlane" : qUnion([Q0])});
            skLineSegment(sketch, "E128.0", {"start": v(35, -113.53) * mm, "end": v(35, -148.53) * mm, "construction": true});
            skLineSegment(sketch, "E129", {"start": v(35, -131.03) * mm, "end": v(-153.9, -131.03) * mm, "construction": true});
            skLineSegment(sketch, "E130.0", {"start": v(35, 168.97) * mm, "end": v(-153.9, 168.97) * mm, "construction": true});
            skLineSegment(sketch, "E131.0", {"start": v(-60, 201.03) * mm, "end": v(60, 201.03) * mm});
            skLineSegment(sketch, "E132", {"start": v(0, 201.03) * mm, "end": v(0, 143.76) * mm, "construction": true});
            skPoint(sketch, "E132.endSnap0", {"position": v(0, 201.03) * mm});
            skArc(sketch, "E133", {"start": v(-22.5, 168.97) * mm, "mid": v(0, 146.47) * mm, "end": v(22.5, 168.97) * mm});
            skLineSegment(sketch, "E134.0", {"start": v(60, 185.97) * mm, "end": v(22.5, 185.97) * mm});
            skLineSegment(sketch, "E135", {"start": v(-22.5, 168.97) * mm, "end": v(-22.5, 185.97) * mm});
            skLineSegment(sketch, "E136", {"start": v(22.5, 168.97) * mm, "end": v(22.5, 185.97) * mm});
            skLineSegment(sketch, "E137.0", {"start": v(60, 201.03) * mm, "end": v(60, 185.97) * mm});
            skLineSegment(sketch, "E138.0", {"start": v(-60, 201.03) * mm, "end": v(-60, 185.97) * mm});
            skPoint(sketch, "E139.orphan", {"position": v(-60, 81.03) * mm});
            skPoint(sketch, "E140.orphan", {"position": v(60, 81.03) * mm});
            skLineSegment(sketch, "E141.trimOffspring", {"start": v(-22.5, 185.97) * mm, "end": v(-60, 185.97) * mm});
            skSolve(sketch);
        }
        {
            var Q0;
            Q0 = qSketchRegion(id + "F40", true);
            extrude(context, id + "F41", {"entities" : qUnion([Q0]), "operationType" : NewBodyOperationType.REMOVE, "endBound" : BoundingType.THROUGH_ALL, "oppositeDirection" : true, "depth" : 25 * mm});
        }
        {
            var Q0;
            Q0=makeQuery(id+"F41.boolean.opBoolean","COPY",FACE,{"derivedFrom":makeQuery(id+"F41.opExtrude","SWEPT_FACE",FACE,{"disambiguationData":[OSD([sQuery(id+"F40.wireOp",EDGE,"E141.trimOffspring")])]})});
            var sketch = newSketch(context, id + "F42", { "sketchPlane" : qUnion([Q0])});
            skLineSegment(sketch, "E142.0", {"start": v(-874.2, 60) * mm, "end": v(-874.2, 22.5) * mm, "construction": true});
            skLineSegment(sketch, "E143.0", {"start": v(-874.2, -60) * mm, "end": v(-925, -60) * mm, "construction": true});
            skLineSegment(sketch, "E144.bottom", {"start": v(-874.2, 60) * mm, "end": v(-880, 60) * mm});
            skLineSegment(sketch, "E144.top", {"start": v(-874.2, -60) * mm, "end": v(-880, -60) * mm});
            skLineSegment(sketch, "E144.left", {"start": v(-874.2, 60) * mm, "end": v(-874.2, -60) * mm});
            skLineSegment(sketch, "E144.right", {"start": v(-880, 60) * mm, "end": v(-880, -60) * mm});
            skLineSegment(sketch, "E145.0", {"start": v(-925, 22.5) * mm, "end": v(-925, 60) * mm, "construction": true});
            skSolve(sketch);
        }
        {
            var Q0;
            Q0 = qSketchRegion(id + "F42", true);
            extrude(context, id + "F43", {"entities" : qUnion([Q0]), "operationType" : NewBodyOperationType.REMOVE, "oppositeDirection" : true, "depth" : 92 * mm});
        }
        {
            var Q0;
            Q0=makeQuery(id+"F41.boolean.opBoolean","COPY",FACE,{"derivedFrom":makeQuery(id+"F41.opExtrude","SWEPT_FACE",FACE,{"disambiguationData":[OSD([sQuery(id+"F40.wireOp",EDGE,"E141.trimOffspring")])]})});
            var sketch = newSketch(context, id + "F44", { "sketchPlane" : qUnion([Q0])});
            skLineSegment(sketch, "E146.0.0", {"start": v(-880, 22.5) * mm, "end": v(-880, 60) * mm, "construction": true});
            skLineSegment(sketch, "E146.0.1", {"start": v(-880, 60) * mm, "end": v(-925, 60) * mm, "construction": true});
            skLineSegment(sketch, "E146.0.2", {"start": v(-925, 60) * mm, "end": v(-925, 22.5) * mm, "construction": true});
            skLineSegment(sketch, "E146.0.3", {"start": v(-925, 22.5) * mm, "end": v(-880, 22.5) * mm, "construction": true});
            skLineSegment(sketch, "E147.0.0", {"start": v(-880, -60) * mm, "end": v(-880, -22.5) * mm, "construction": true});
            skLineSegment(sketch, "E147.0.1", {"start": v(-880, -22.5) * mm, "end": v(-925, -22.5) * mm, "construction": true});
            skLineSegment(sketch, "E147.0.2", {"start": v(-925, -22.5) * mm, "end": v(-925, -60) * mm, "construction": true});
            skLineSegment(sketch, "E147.0.3", {"start": v(-925, -60) * mm, "end": v(-880, -60) * mm, "construction": true});
            skLineSegment(sketch, "E148", {"start": v(-902.5, 60) * mm, "end": v(-902.5, -60) * mm, "construction": true});
            skLineSegment(sketch, "E149", {"start": v(-902.5, 0) * mm, "end": v(-937.6, 0) * mm, "construction": true});
            skLineSegment(sketch, "E150.0", {"start": v(-902.5, 37.5) * mm, "end": v(-937.6, 37.5) * mm, "construction": true});
            skPoint(sketch, "E151", {"position": v(-902.5, 37.5) * mm});
            skPoint(sketch, "E152.MirrorP", {"position": v(-902.5, -37.5) * mm});
            skSolve(sketch);
        }
        {
            var Q0;
            Q0=sQuery(id+"F44.wireOp",VERTEX,"E151");
            var Q1;
            Q1=sQuery(id+"F44.wireOp",VERTEX,"E152.MirrorP");
            var Q2;
            Q2=makeQuery(id+"F39.opExtrude","SWEPT_BODY",BODY,{"disambiguationData":[OSD([sQuery(id+"F38.wireOp",EDGE,"E127.bottom"),sQuery(id+"F38.wireOp",EDGE,"E127.top"),sQuery(id+"F38.wireOp",EDGE,"E127.left"),sQuery(id+"F38.wireOp",EDGE,"E127.right")])]});
            hole(context, id + "F45", {"style" : HoleStyle.SIMPLE, "endStyle" : HoleEndStyle.BLIND, "standardTappedOrClearance" : lookupTablePath({ "standard" : "ISO", "engagement" : "75%", "pitch" : "1.25 mm", "size" : "M12", "type" : "Tapped" }), "standardBlindInLast" : lookupTablePath({ "standard" : "ISO", "engagement" : "75%", "pitch" : "1.25 mm", "size" : "M12", "type" : "Tapped" }), "holeDiameter" : 10.8 * mm, "holeDepth" : 35 * mm, "locations" : qUnion([Q0, Q1]), "scope" : qUnion([Q2]), "majorDiameter" : 12 * mm});
        }
        {
            var Q0;
            Q0=makeQuery(id+"F39.opExtrude","SWEPT_BODY",BODY,{"disambiguationData":[OSD([sQuery(id+"F38.wireOp",EDGE,"E127.bottom"),sQuery(id+"F38.wireOp",EDGE,"E127.top"),sQuery(id+"F38.wireOp",EDGE,"E127.left"),sQuery(id+"F38.wireOp",EDGE,"E127.right")])]});
            var Q1;
            Q1=qCreatedBy(makeId("Right.planeOp"),FACE);
            mirror(context, id + "F46", {"entities" : qUnion([Q0]), "mirrorPlane" : qUnion([Q1])});
        }
        {
            var Q0;
            Q0=qCreatedBy(makeId("Right.planeOp"),FACE);
            cPlane(context, id + "F47", {"entities" : qUnion([Q0]), "cplaneType" : CPlaneType.OFFSET, "offset" : (330 / 2 + 15) * mm, "width" : 150 * mm, "height" : 150 * mm});
        }
        {
            var Q0;
            Q0=qCreatedBy(id+"F47.planeOp",FACE);
            var sketch = newSketch(context, id + "F48", { "sketchPlane" : qUnion([Q0])});
            skLineSegment(sketch, "E153", {"start": v(0, 256.72) * mm, "end": v(0, -431.7) * mm, "construction": true});
            skLineSegment(sketch, "E154.0.0", {"start": v(-60, 81.03) * mm, "end": v(-60, 185.97) * mm, "construction": true});
            skLineSegment(sketch, "E154.0.1", {"start": v(-60, 185.97) * mm, "end": v(-22.5, 185.97) * mm, "construction": true});
            skLineSegment(sketch, "E154.0.2", {"start": v(-22.5, 185.97) * mm, "end": v(-22.5, 168.97) * mm, "construction": true});
            skArc(sketch, "E154.0.3", {"start": v(-22.5, 168.97) * mm, "mid": v(0, 146.47) * mm, "end": v(22.5, 168.97) * mm, "construction": true});
            skLineSegment(sketch, "E154.0.4", {"start": v(22.5, 168.97) * mm, "end": v(22.5, 185.97) * mm, "construction": true});
            skLineSegment(sketch, "E154.0.5", {"start": v(22.5, 185.97) * mm, "end": v(144, 185.97) * mm, "construction": true});
            skLineSegment(sketch, "E154.0.6", {"start": v(60, 185.97) * mm, "end": v(60, 81.03) * mm, "construction": true});
            skLineSegment(sketch, "E154.0.7", {"start": v(60, 81.03) * mm, "end": v(-60, 81.03) * mm, "construction": true});
            skLineSegment(sketch, "E155.0", {"start": v(144, 256.72) * mm, "end": v(144, -69.47) * mm});
            skLineSegment(sketch, "E156.0.0", {"start": v(77.22, 81.03) * mm, "end": v(77.22, 69.47) * mm, "construction": true});
            skLineSegment(sketch, "E156.0.1", {"start": v(77.22, 69.47) * mm, "end": v(-77.22, 69.47) * mm, "construction": true});
            skLineSegment(sketch, "E156.0.2", {"start": v(-77.22, 69.47) * mm, "end": v(-77.22, 81.03) * mm, "construction": true});
            skLineSegment(sketch, "E156.0.3", {"start": v(-77.22, 81.03) * mm, "end": v(77.22, 81.03) * mm, "construction": true});
            skLineSegment(sketch, "E157.0.0", {"start": v(-77.22, -69.47) * mm, "end": v(144, -69.47) * mm, "construction": true});
            skLineSegment(sketch, "E157.0.1", {"start": v(77.22, -69.47) * mm, "end": v(77.22, -81.03) * mm, "construction": true});
            skLineSegment(sketch, "E157.0.2", {"start": v(77.22, -81.03) * mm, "end": v(-77.22, -81.03) * mm, "construction": true});
            skLineSegment(sketch, "E157.0.3", {"start": v(-77.22, -81.03) * mm, "end": v(-77.22, -69.47) * mm, "construction": true});
            skLineSegment(sketch, "E158.0.0", {"start": v(16.76, -69.47) * mm, "end": v(-16.76, -69.47) * mm, "construction": true});
            skArc(sketch, "E158.0.1", {"start": v(-16.76, -69.47) * mm, "mid": v(-7.78, -65.75) * mm, "end": v(-4.06, -56.77) * mm, "construction": true});
            skLineSegment(sketch, "E158.0.2", {"start": v(-4.06, -56.77) * mm, "end": v(-4.06, 56.77) * mm, "construction": true});
            skArc(sketch, "E158.0.3", {"start": v(-4.06, 56.77) * mm, "mid": v(-7.78, 65.75) * mm, "end": v(-16.76, 69.47) * mm, "construction": true});
            skLineSegment(sketch, "E158.0.4", {"start": v(-16.76, 69.47) * mm, "end": v(16.76, 69.47) * mm, "construction": true});
            skArc(sketch, "E158.0.5", {"start": v(16.76, 69.47) * mm, "mid": v(7.78, 65.75) * mm, "end": v(4.06, 56.77) * mm, "construction": true});
            skLineSegment(sketch, "E158.0.6", {"start": v(4.06, 56.77) * mm, "end": v(4.06, -56.77) * mm, "construction": true});
            skArc(sketch, "E158.0.7", {"start": v(4.06, -56.77) * mm, "mid": v(7.78, -65.75) * mm, "end": v(16.76, -69.47) * mm, "construction": true});
            skLineSegment(sketch, "E159", {"start": v(144, 185.97) * mm, "end": v(77.22, 197.75) * mm});
            skLineSegment(sketch, "E160.0", {"start": v(70, 86.03) * mm, "end": v(77.22, 86.03) * mm, "construction": true});
            skLineSegment(sketch, "E161.0", {"start": v(77.22, 199.02) * mm, "end": v(77.22, 69.47) * mm});
            skLineSegment(sketch, "E162", {"start": v(144, 30.53) * mm, "end": v(80.74, -69.47) * mm});
            skLineSegment(sketch, "E163", {"start": v(80.74, -69.47) * mm, "end": v(16.76, -69.47) * mm});
            skLineSegment(sketch, "E164", {"start": v(16.76, -69.47) * mm, "end": v(4.06, -56.77) * mm});
            skLineSegment(sketch, "E165", {"start": v(4.06, -56.77) * mm, "end": v(4.06, 56.77) * mm});
            skLineSegment(sketch, "E166", {"start": v(4.06, 56.77) * mm, "end": v(16.76, 69.47) * mm});
            skLineSegment(sketch, "E167", {"start": v(16.76, 69.47) * mm, "end": v(77.22, 69.47) * mm});
            skLineSegment(sketch, "E168", {"start": v(77.22, 69.47) * mm, "end": v(77.22, 86.03) * mm});
            skLineSegment(sketch, "E169", {"start": v(77.22, 86.03) * mm, "end": v(70, 86.03) * mm});
            skLineSegment(sketch, "E170", {"start": v(70, 185.97) * mm, "end": v(70, 199.02) * mm});
            skLineSegment(sketch, "E171", {"start": v(144, 185.97) * mm, "end": v(144, 30.53) * mm});
            skLineSegment(sketch, "E172", {"start": v(77.22, 199.02) * mm, "end": v(91.33, 199.02) * mm});
            skLineSegment(sketch, "E173", {"start": v(77.22, 199.02) * mm, "end": v(150.28, 186.14) * mm});
            skSolve(sketch);
        }
        {
            var Q0;
            Q0 = qSketchRegion(id + "F48", true);
            extrude(context, id + "F49", {"entities" : qUnion([Q0]), "oppositeDirection" : true, "depth" : 15.88 * mm});
        }
        {
            var Q0;
            Q0=makeQuery(id+"F49.opExtrude","CAP_FACE",FACE,{"disambiguationData":[OSD([sQuery(id+"F48.wireOp",EDGE,"E159"),sQuery(id+"F48.wireOp",EDGE,"E162"),sQuery(id+"F48.wireOp",EDGE,"E163"),sQuery(id+"F48.wireOp",EDGE,"E164"),sQuery(id+"F48.wireOp",EDGE,"E165"),sQuery(id+"F48.wireOp",EDGE,"E166"),sQuery(id+"F48.wireOp",EDGE,"E167"),sQuery(id+"F48.wireOp",EDGE,"E168"),sQuery(id+"F48.wireOp",EDGE,"E169"),sQuery(id+"F48.wireOp",EDGE,"E170"),sQuery(id+"F48.wireOp",EDGE,"E171")])],"isStart":true});
            var sketch = newSketch(context, id + "F50", { "sketchPlane" : qUnion([Q0])});
            skLineSegment(sketch, "E174.0.4", {"start": v(80.74, -69.47) * mm, "end": v(144, 30.53) * mm});
            skLineSegment(sketch, "E174.0.5", {"start": v(16.76, -69.47) * mm, "end": v(80.74, -69.47) * mm});
            skLineSegment(sketch, "E174.0.6", {"start": v(4.06, -56.77) * mm, "end": v(16.76, -69.47) * mm});
            skLineSegment(sketch, "E174.0.7", {"start": v(4.06, 56.77) * mm, "end": v(4.06, -56.77) * mm});
            skLineSegment(sketch, "E174.0.8", {"start": v(16.76, 69.47) * mm, "end": v(4.06, 56.77) * mm});
            skLineSegment(sketch, "E174.0.9", {"start": v(77.22, 69.47) * mm, "end": v(16.76, 69.47) * mm});
            skLineSegment(sketch, "E174.0.10", {"start": v(77.22, 86.03) * mm, "end": v(77.22, 69.47) * mm});
            skLineSegment(sketch, "E175.0.0", {"start": v(144, 187.25) * mm, "end": v(77.22, 199.02) * mm});
            skLineSegment(sketch, "E175.0.1", {"start": v(77.22, 199.02) * mm, "end": v(77.22, 137.25) * mm});
            skLineSegment(sketch, "E175.0.8", {"start": v(144, 137.25) * mm, "end": v(144, 187.25) * mm});
            skLineSegment(sketch, "E176", {"start": v(77.22, 137.25) * mm, "end": v(144, 137.25) * mm});
            skSolve(sketch);
        }
        {
            var Q0;
            Q0 = qSketchRegion(id + "F50", true);
            extrude(context, id + "F51", {"entities" : qUnion([Q0]), "depth" : 19 * mm});
        }
        {
            var Q0;
            Q0=makeQuery(id+"F51.opExtrude","SWEPT_FACE",FACE,{"disambiguationData":[OSD([sQuery(id+"F50.wireOp",EDGE,"E175.0.0")])]});
            var sketch = newSketch(context, id + "F52", { "sketchPlane" : qUnion([Q0])});
            skLineSegment(sketch, "E177", {"start": v(0, 185.79) * mm, "end": v(0, -149.3) * mm, "construction": true});
            skLineSegment(sketch, "E178.0", {"start": v(190, 185.79) * mm, "end": v(190, -149.3) * mm, "construction": true});
            skLineSegment(sketch, "E179.0.0", {"start": v(180, 109.52) * mm, "end": v(180, 34.38) * mm, "construction": true});
            skLineSegment(sketch, "E179.0.1", {"start": v(180, 34.38) * mm, "end": v(205.4, 34.38) * mm, "construction": true});
            skLineSegment(sketch, "E179.0.2", {"start": v(205.4, 34.38) * mm, "end": v(205.4, 109.52) * mm, "construction": true});
            skLineSegment(sketch, "E179.0.3", {"start": v(205.4, 109.52) * mm, "end": v(180, 109.52) * mm, "construction": true});
            skLineSegment(sketch, "E180.0", {"start": v(205.4, 69.52) * mm, "end": v(180, 69.52) * mm, "construction": true});
            skLineSegment(sketch, "E181.0", {"start": v(205.4, 94.52) * mm, "end": v(180, 94.52) * mm, "construction": true});
            skPoint(sketch, "E182", {"position": v(190, 94.52) * mm});
            skPoint(sketch, "E183", {"position": v(190, 69.52) * mm});
            skSolve(sketch);
        }
        {
            var Q0;
            Q0=sQuery(id+"F52.wireOp",VERTEX,"E182");
            var Q1;
            Q1=sQuery(id+"F52.wireOp",VERTEX,"E183");
            var Q2;
            Q2=makeQuery(id+"F51.opExtrude","SWEPT_BODY",BODY,{"disambiguationData":[OSD([sQuery(id+"F50.wireOp",EDGE,"E175.0.0"),sQuery(id+"F50.wireOp",EDGE,"E175.0.1"),sQuery(id+"F50.wireOp",EDGE,"E175.0.8"),sQuery(id+"F50.wireOp",EDGE,"E176")])]});
            hole(context, id + "F53", {"style" : HoleStyle.SIMPLE, "endStyle" : HoleEndStyle.BLIND, "standardTappedOrClearance" : lookupTablePath({ "standard" : "ISO", "engagement" : "75%", "pitch" : "1.5 mm", "size" : "M12", "type" : "Tapped" }), "standardBlindInLast" : lookupTablePath({ "standard" : "ISO", "engagement" : "75%", "pitch" : "1.5 mm", "size" : "M12", "type" : "Tapped" }), "holeDiameter" : 10.5 * mm, "holeDepth" : 30 * mm, "locations" : qUnion([Q0, Q1]), "scope" : qUnion([Q2]), "majorDiameter" : 12 * mm});
        }
        {
            var Q0;
            Q0=makeQuery(id+"F49.opExtrude","SWEPT_BODY",BODY,{"disambiguationData":[OSD([sQuery(id+"F48.wireOp",EDGE,"E159"),sQuery(id+"F48.wireOp",EDGE,"E162"),sQuery(id+"F48.wireOp",EDGE,"E163"),sQuery(id+"F48.wireOp",EDGE,"E164"),sQuery(id+"F48.wireOp",EDGE,"E165"),sQuery(id+"F48.wireOp",EDGE,"E166"),sQuery(id+"F48.wireOp",EDGE,"E167"),sQuery(id+"F48.wireOp",EDGE,"E168"),sQuery(id+"F48.wireOp",EDGE,"E169"),sQuery(id+"F48.wireOp",EDGE,"E170"),sQuery(id+"F48.wireOp",EDGE,"E171")])]});
            var Q1;
            Q1=makeQuery(id+"Fl3NnRKCw4Xixsh_5.opExtrude","SWEPT_BODY",BODY,{"disambiguationData":[OSD([sQuery(id+"F50.wireOp",EDGE,"E174.0.2"),sQuery(id+"F50.wireOp",EDGE,"L5QzTxGx-Pnf6-FATO-cNnD-iBCD0eLFIrfw"),sQuery(id+"F50.wireOp",EDGE,"wuJ0hKJl-j7K5-ufxr-qZVR-Fc0DleJu5Dkg"),sQuery(id+"F50.wireOp",EDGE,"Ftl8TeeW-pfTl-imrB-EIy6-TxBNQzbVambr")])]});
            var Q2;
            Q2=qCreatedBy(makeId("Right.planeOp"),FACE);
            mirror(context, id + "F54", {"entities" : qUnion([Q0, Q1]), "mirrorPlane" : qUnion([Q2])});
        }
        {
            var Q0;
            Q0=qCreatedBy(id+"F47.planeOp",FACE);
            cPlane(context, id + "F55", {"entities" : qUnion([Q0]), "cplaneType" : CPlaneType.OFFSET, "offset" : 350 * mm, "width" : 150 * mm, "height" : 150 * mm});
        }
        {
            var Q0;
            Q0=makeQuery(id+"F49.opExtrude","SWEPT_BODY",BODY,{"disambiguationData":[OSD([sQuery(id+"F48.wireOp",EDGE,"E159"),sQuery(id+"F48.wireOp",EDGE,"E162"),sQuery(id+"F48.wireOp",EDGE,"E163"),sQuery(id+"F48.wireOp",EDGE,"E164"),sQuery(id+"F48.wireOp",EDGE,"E165"),sQuery(id+"F48.wireOp",EDGE,"E166"),sQuery(id+"F48.wireOp",EDGE,"E167"),sQuery(id+"F48.wireOp",EDGE,"E168"),sQuery(id+"F48.wireOp",EDGE,"E169"),sQuery(id+"F48.wireOp",EDGE,"E170"),sQuery(id+"F48.wireOp",EDGE,"E171")])]});
            var Q1;
            Q1=makeQuery(id+"Fl3NnRKCw4Xixsh_5.opExtrude","SWEPT_BODY",BODY,{"disambiguationData":[OSD([sQuery(id+"F50.wireOp",EDGE,"E174.0.2"),sQuery(id+"F50.wireOp",EDGE,"L5QzTxGx-Pnf6-FATO-cNnD-iBCD0eLFIrfw"),sQuery(id+"F50.wireOp",EDGE,"wuJ0hKJl-j7K5-ufxr-qZVR-Fc0DleJu5Dkg"),sQuery(id+"F50.wireOp",EDGE,"Ftl8TeeW-pfTl-imrB-EIy6-TxBNQzbVambr")])]});
            var Q2;
            Q2=qCreatedBy(id+"F55.planeOp",FACE);
            mirror(context, id + "F56", {"entities" : qUnion([Q0, Q1]), "mirrorPlane" : qUnion([Q2])});
        }
        {
            var Q0;
            Q0=makeQuery(id+"F56.opPattern","COPY",BODY,{"derivedFrom":makeQuery(id+"F49.opExtrude","SWEPT_BODY",BODY,{"disambiguationData":[OSD([sQuery(id+"F48.wireOp",EDGE,"E159"),sQuery(id+"F48.wireOp",EDGE,"E162"),sQuery(id+"F48.wireOp",EDGE,"E163"),sQuery(id+"F48.wireOp",EDGE,"E164"),sQuery(id+"F48.wireOp",EDGE,"E165"),sQuery(id+"F48.wireOp",EDGE,"E166"),sQuery(id+"F48.wireOp",EDGE,"E167"),sQuery(id+"F48.wireOp",EDGE,"E168"),sQuery(id+"F48.wireOp",EDGE,"E169"),sQuery(id+"F48.wireOp",EDGE,"E170"),sQuery(id+"F48.wireOp",EDGE,"E171")])]}),"instanceName":"1"});
            var Q1;
            Q1=makeQuery(id+"F56.opPattern","COPY",BODY,{"derivedFrom":makeQuery(id+"Fl3NnRKCw4Xixsh_5.opExtrude","SWEPT_BODY",BODY,{"disambiguationData":[OSD([sQuery(id+"F50.wireOp",EDGE,"E174.0.2"),sQuery(id+"F50.wireOp",EDGE,"L5QzTxGx-Pnf6-FATO-cNnD-iBCD0eLFIrfw"),sQuery(id+"F50.wireOp",EDGE,"wuJ0hKJl-j7K5-ufxr-qZVR-Fc0DleJu5Dkg"),sQuery(id+"F50.wireOp",EDGE,"Ftl8TeeW-pfTl-imrB-EIy6-TxBNQzbVambr")])]}),"instanceName":"1"});
            var Q2;
            Q2=qCreatedBy(makeId("Right.planeOp"),FACE);
            mirror(context, id + "F57", {"entities" : qUnion([Q0, Q1]), "mirrorPlane" : qUnion([Q2])});
        }
        {
            var Q0;
            Q0=qCreatedBy(id+"F47.planeOp",FACE);
            var sketch = newSketch(context, id + "F58", { "sketchPlane" : qUnion([Q0])});
            skLineSegment(sketch, "E184", {"start": v(0, 263.92) * mm, "end": v(0, -250.39) * mm, "construction": true});
            skLineSegment(sketch, "E185.0", {"start": v(-206, 263.92) * mm, "end": v(-206, -250.39) * mm, "construction": true});
            skLineSegment(sketch, "E186.0.0", {"start": v(77.22, 81.03) * mm, "end": v(77.22, 69.47) * mm, "construction": true});
            skLineSegment(sketch, "E186.0.1", {"start": v(77.22, 69.47) * mm, "end": v(-77.22, 69.47) * mm, "construction": true});
            skLineSegment(sketch, "E186.0.2", {"start": v(-77.22, 69.47) * mm, "end": v(-77.22, 81.03) * mm, "construction": true});
            skLineSegment(sketch, "E186.0.3", {"start": v(-77.22, 81.03) * mm, "end": v(77.22, 81.03) * mm, "construction": true});
            skLineSegment(sketch, "E187.0.0", {"start": v(16.76, -69.47) * mm, "end": v(-16.76, -69.47) * mm, "construction": true});
            skArc(sketch, "E187.0.1", {"start": v(-16.76, -69.47) * mm, "mid": v(-7.78, -65.75) * mm, "end": v(-4.06, -56.77) * mm, "construction": true});
            skLineSegment(sketch, "E187.0.2", {"start": v(-4.06, -56.77) * mm, "end": v(-4.06, 56.77) * mm, "construction": true});
            skArc(sketch, "E187.0.3", {"start": v(-4.06, 56.77) * mm, "mid": v(-7.78, 65.75) * mm, "end": v(-16.76, 69.47) * mm, "construction": true});
            skLineSegment(sketch, "E187.0.4", {"start": v(-16.76, 69.47) * mm, "end": v(16.76, 69.47) * mm, "construction": true});
            skArc(sketch, "E187.0.5", {"start": v(16.76, 69.47) * mm, "mid": v(7.78, 65.75) * mm, "end": v(4.06, 56.77) * mm, "construction": true});
            skLineSegment(sketch, "E187.0.6", {"start": v(4.06, 56.77) * mm, "end": v(4.06, -56.77) * mm, "construction": true});
            skArc(sketch, "E187.0.7", {"start": v(4.06, -56.77) * mm, "mid": v(7.78, -65.75) * mm, "end": v(16.76, -69.47) * mm, "construction": true});
            skLineSegment(sketch, "E188.0.0", {"start": v(-77.22, -69.47) * mm, "end": v(77.22, -69.47) * mm, "construction": true});
            skLineSegment(sketch, "E188.0.1", {"start": v(77.22, -69.47) * mm, "end": v(77.22, -81.03) * mm, "construction": true});
            skLineSegment(sketch, "E188.0.2", {"start": v(77.22, -81.03) * mm, "end": v(-77.22, -81.03) * mm, "construction": true});
            skLineSegment(sketch, "E188.0.3", {"start": v(-77.22, -81.03) * mm, "end": v(-77.22, -69.47) * mm, "construction": true});
            skLineSegment(sketch, "E189.0", {"start": v(-206, 10.53) * mm, "end": v(77.22, 10.53) * mm, "construction": true});
            skLineSegment(sketch, "E190", {"start": v(-77.22, 69.47) * mm, "end": v(-16.76, 69.47) * mm});
            skLineSegment(sketch, "E191", {"start": v(-16.76, 69.47) * mm, "end": v(-4.06, 56.77) * mm});
            skLineSegment(sketch, "E192", {"start": v(-4.06, 56.77) * mm, "end": v(-4.06, -56.77) * mm});
            skLineSegment(sketch, "E193", {"start": v(-16.76, -69.47) * mm, "end": v(-4.06, -56.77) * mm});
            skLineSegment(sketch, "E194", {"start": v(-16.76, -69.47) * mm, "end": v(-77.22, -69.47) * mm});
            skLineSegment(sketch, "E195", {"start": v(-77.22, -69.47) * mm, "end": v(-206, 10.53) * mm});
            skLineSegment(sketch, "E196", {"start": v(-77.22, 69.47) * mm, "end": v(-77.22, 185.97) * mm});
            skLineSegment(sketch, "E197.0.0", {"start": v(-60, 81.03) * mm, "end": v(-60, 185.97) * mm});
            skLineSegment(sketch, "E197.0.1", {"start": v(-60, 185.97) * mm, "end": v(-22.5, 185.97) * mm});
            skLineSegment(sketch, "E197.0.2", {"start": v(-22.5, 185.97) * mm, "end": v(-22.5, 168.97) * mm});
            skArc(sketch, "E197.0.3", {"start": v(-22.5, 168.97) * mm, "mid": v(0, 146.47) * mm, "end": v(22.5, 168.97) * mm});
            skLineSegment(sketch, "E197.0.4", {"start": v(22.5, 168.97) * mm, "end": v(22.5, 185.97) * mm});
            skLineSegment(sketch, "E197.0.7", {"start": v(60, 81.03) * mm, "end": v(-60, 81.03) * mm});
            skPoint(sketch, "E197.0.6.start.orphan", {"position": v(60, 185.97) * mm});
            skLineSegment(sketch, "E198", {"start": v(-77.22, 185.97) * mm, "end": v(-222.54, 185.97) * mm, "construction": true});
            skLineSegment(sketch, "E199", {"start": v(-77.22, 185.97) * mm, "end": v(-206, 111.62) * mm});
            skLineSegment(sketch, "E200", {"start": v(-206, 111.62) * mm, "end": v(-206, 10.53) * mm});
            skSolve(sketch);
        }
        {
            var Q0;
            Q0 = qSketchRegion(id + "F58", true);
            extrude(context, id + "F59", {"entities" : qUnion([Q0]), "oppositeDirection" : true, "depth" : 16 * mm});
        }
        {
            var Q0;
            Q0=makeQuery(id+"F59.opExtrude","CAP_FACE",FACE,{"disambiguationData":[OSD([sQuery(id+"F58.wireOp",EDGE,"E190"),sQuery(id+"F58.wireOp",EDGE,"E191"),sQuery(id+"F58.wireOp",EDGE,"E192"),sQuery(id+"F58.wireOp",EDGE,"E193"),sQuery(id+"F58.wireOp",EDGE,"E194"),sQuery(id+"F58.wireOp",EDGE,"E195"),sQuery(id+"F58.wireOp",EDGE,"E196"),sQuery(id+"F58.wireOp",EDGE,"E199"),sQuery(id+"F58.wireOp",EDGE,"E200")])],"isStart":false});
            var sketch = newSketch(context, id + "F60", { "sketchPlane" : qUnion([Q0])});
            skLineSegment(sketch, "E201.0.0", {"start": v(206, 111.62) * mm, "end": v(77.22, 185.97) * mm, "construction": true});
            skLineSegment(sketch, "E201.0.1", {"start": v(77.22, 185.97) * mm, "end": v(77.22, 69.47) * mm, "construction": true});
            skLineSegment(sketch, "E201.0.2", {"start": v(77.22, 69.47) * mm, "end": v(16.76, 69.47) * mm, "construction": true});
            skLineSegment(sketch, "E201.0.3", {"start": v(16.76, 69.47) * mm, "end": v(4.06, 56.77) * mm, "construction": true});
            skLineSegment(sketch, "E201.0.4", {"start": v(4.06, 56.77) * mm, "end": v(4.06, -56.77) * mm, "construction": true});
            skLineSegment(sketch, "E201.0.5", {"start": v(4.06, -56.77) * mm, "end": v(16.76, -69.47) * mm, "construction": true});
            skLineSegment(sketch, "E201.0.6", {"start": v(16.76, -69.47) * mm, "end": v(77.22, -69.47) * mm, "construction": true});
            skLineSegment(sketch, "E201.0.7", {"start": v(77.22, -69.47) * mm, "end": v(206, 10.53) * mm, "construction": true});
            skLineSegment(sketch, "E201.0.8", {"start": v(206, 10.53) * mm, "end": v(206, 111.62) * mm, "construction": true});
            skLineSegment(sketch, "E202.0", {"start": v(191, 85.64) * mm, "end": v(62.22, 160) * mm, "construction": true});
            skLineSegment(sketch, "E203", {"start": v(191, 85.64) * mm, "end": v(206, 111.62) * mm, "construction": true});
            skLineSegment(sketch, "E204.0", {"start": v(178, 93.14) * mm, "end": v(193, 119.12) * mm, "construction": true});
            skLineSegment(sketch, "E205.0", {"start": v(100.07, 138.14) * mm, "end": v(115.07, 164.12) * mm, "construction": true});
            skPoint(sketch, "E206", {"position": v(100.07, 138.14) * mm});
            skPoint(sketch, "E207", {"position": v(178, 93.14) * mm});
            skSolve(sketch);
        }
        {
            var Q0;
            Q0=sQuery(id+"F60.wireOp",VERTEX,"E206");
            var Q1;
            Q1=sQuery(id+"F60.wireOp",VERTEX,"E207");
            var Q2;
            Q2=makeQuery(id+"F59.opExtrude","SWEPT_BODY",BODY,{"disambiguationData":[OSD([sQuery(id+"F58.wireOp",EDGE,"E190"),sQuery(id+"F58.wireOp",EDGE,"E191"),sQuery(id+"F58.wireOp",EDGE,"E192"),sQuery(id+"F58.wireOp",EDGE,"E193"),sQuery(id+"F58.wireOp",EDGE,"E194"),sQuery(id+"F58.wireOp",EDGE,"E195"),sQuery(id+"F58.wireOp",EDGE,"E196"),sQuery(id+"F58.wireOp",EDGE,"E199"),sQuery(id+"F58.wireOp",EDGE,"E200")])]});
            hole(context, id + "F61", {"style" : HoleStyle.SIMPLE, "endStyle" : HoleEndStyle.BLIND, "standardTappedOrClearance" : lookupTablePath({ "standard" : "ISO", "size" : "12", "type" : "Drilled" }), "standardBlindInLast" : lookupTablePath({ "standard" : "ISO", "size" : "12", "type" : "Drilled" }), "holeDiameter" : 12 * mm, "holeDepth" : 30 * mm, "locations" : qUnion([Q0, Q1]), "scope" : qUnion([Q2])});
        }
        {
            var Q0;
            Q0=makeQuery(id+"F59.opExtrude","SWEPT_BODY",BODY,{"disambiguationData":[OSD([sQuery(id+"F58.wireOp",EDGE,"E190"),sQuery(id+"F58.wireOp",EDGE,"E191"),sQuery(id+"F58.wireOp",EDGE,"E192"),sQuery(id+"F58.wireOp",EDGE,"E193"),sQuery(id+"F58.wireOp",EDGE,"E194"),sQuery(id+"F58.wireOp",EDGE,"E195"),sQuery(id+"F58.wireOp",EDGE,"E196"),sQuery(id+"F58.wireOp",EDGE,"E199"),sQuery(id+"F58.wireOp",EDGE,"E200")])]});
            var Q1;
            Q1=qCreatedBy(makeId("Right.planeOp"),FACE);
            mirror(context, id + "F62", {"entities" : qUnion([Q0]), "mirrorPlane" : qUnion([Q1])});
        }
        {
            var Q0;
            Q0=makeQuery(id+"F59.opExtrude","SWEPT_BODY",BODY,{"disambiguationData":[OSD([sQuery(id+"F58.wireOp",EDGE,"E190"),sQuery(id+"F58.wireOp",EDGE,"E191"),sQuery(id+"F58.wireOp",EDGE,"E192"),sQuery(id+"F58.wireOp",EDGE,"E193"),sQuery(id+"F58.wireOp",EDGE,"E194"),sQuery(id+"F58.wireOp",EDGE,"E195"),sQuery(id+"F58.wireOp",EDGE,"E196"),sQuery(id+"F58.wireOp",EDGE,"E199"),sQuery(id+"F58.wireOp",EDGE,"E200")])]});
            var Q1;
            Q1=qCreatedBy(id+"F55.planeOp",FACE);
            mirror(context, id + "F63", {"entities" : qUnion([Q0]), "mirrorPlane" : qUnion([Q1])});
        }
        {
            var Q0;
            Q0=makeQuery(id+"F63.opPattern","COPY",BODY,{"derivedFrom":makeQuery(id+"F59.opExtrude","SWEPT_BODY",BODY,{"disambiguationData":[OSD([sQuery(id+"F58.wireOp",EDGE,"E190"),sQuery(id+"F58.wireOp",EDGE,"E191"),sQuery(id+"F58.wireOp",EDGE,"E192"),sQuery(id+"F58.wireOp",EDGE,"E193"),sQuery(id+"F58.wireOp",EDGE,"E194"),sQuery(id+"F58.wireOp",EDGE,"E195"),sQuery(id+"F58.wireOp",EDGE,"E196"),sQuery(id+"F58.wireOp",EDGE,"E199"),sQuery(id+"F58.wireOp",EDGE,"E200")])]}),"instanceName":"1"});
            var Q1;
            Q1=qCreatedBy(makeId("Right.planeOp"),FACE);
            mirror(context, id + "F64", {"operationType" : NewBodyOperationType.ADD, "entities" : qUnion([Q0]), "mirrorPlane" : qUnion([Q1])});
        }
        {
            var Q0;
            Q0=makeQuery(id+"F5.opExtrude","SWEPT_EDGE",EDGE,{"disambiguationData":[OSD([sQuery(id+"F4.wireOp",EDGE,"E50.bottom"),sQuery(id+"F4.wireOp",EDGE,"E50.right")])]});
            var Q1;
            Q1=makeQuery(id+"F5.opExtrude","SWEPT_EDGE",EDGE,{"disambiguationData":[OSD([sQuery(id+"F4.wireOp",EDGE,"E50.top"),sQuery(id+"F4.wireOp",EDGE,"E52.trimOffspring")])]});
            chamfer(context, id + "F65", {"entities" : qUnion([Q0, Q1]), "width" : 5 * mm, "tangentPropagation" : true});
        }
        {
            var Q0;
            Q0=makeQuery(id+"F29.opPattern","COPY",EDGE,{"derivedFrom":makeQuery(id+"F5.opExtrude","SWEPT_EDGE",EDGE,{"disambiguationData":[OSD([sQuery(id+"F4.wireOp",EDGE,"E50.bottom"),sQuery(id+"F4.wireOp",EDGE,"E50.right")])]}),"instanceName":"1"});
            var Q1;
            Q1=makeQuery(id+"F29.opPattern","COPY",EDGE,{"derivedFrom":makeQuery(id+"F5.opExtrude","SWEPT_EDGE",EDGE,{"disambiguationData":[OSD([sQuery(id+"F4.wireOp",EDGE,"E50.top"),sQuery(id+"F4.wireOp",EDGE,"E52.trimOffspring")])]}),"instanceName":"1"});
            chamfer(context, id + "F66", {"entities" : qUnion([Q0, Q1]), "width" : 5 * mm, "tangentPropagation" : true});
        }
        {
            var Q0;
            Q0=makeQuery(id+"F63.opPattern","COPY",FACE,{"derivedFrom":makeQuery(id+"F59.opExtrude","CAP_FACE",FACE,{"disambiguationData":[OSD([sQuery(id+"F58.wireOp",EDGE,"E190"),sQuery(id+"F58.wireOp",EDGE,"E191"),sQuery(id+"F58.wireOp",EDGE,"E192"),sQuery(id+"F58.wireOp",EDGE,"E193"),sQuery(id+"F58.wireOp",EDGE,"E194"),sQuery(id+"F58.wireOp",EDGE,"E195"),sQuery(id+"F58.wireOp",EDGE,"E196"),sQuery(id+"F58.wireOp",EDGE,"E199"),sQuery(id+"F58.wireOp",EDGE,"E200")])],"isStart":false}),"instanceName":"1"});
            var sketch = newSketch(context, id + "F67", { "sketchPlane" : qUnion([Q0])});
            skLineSegment(sketch, "E208.0", {"start": v(-35, -113.53) * mm, "end": v(-35, -148.53) * mm, "construction": true});
            skLineSegment(sketch, "E209", {"start": v(-35, -131.03) * mm, "end": v(-367.6, -131.03) * mm, "construction": true});
            skLineSegment(sketch, "E210.0", {"start": v(-35, -16.03) * mm, "end": v(-367.6, -16.03) * mm, "construction": true});
            skLineSegment(sketch, "E211.0", {"start": v(-35, 23.97) * mm, "end": v(-367.6, 23.97) * mm, "construction": true});
            skLineSegment(sketch, "E212", {"start": v(0, 332.63) * mm, "end": v(0, -263.23) * mm, "construction": true});
            skLineSegment(sketch, "E213.0", {"start": v(-140, 23.97) * mm, "end": v(-140, -16.03) * mm, "construction": true});
            skLineSegment(sketch, "E214.trimOffspring", {"start": v(-140, -131.03) * mm, "end": v(-140, -263.23) * mm, "construction": true});
            skLineSegment(sketch, "E215.bottom", {"start": v(-160, 23.97) * mm, "end": v(-120, 23.97) * mm});
            skLineSegment(sketch, "E215.top", {"start": v(-160, -16.03) * mm, "end": v(-120, -16.03) * mm});
            skLineSegment(sketch, "E215.left", {"start": v(-160, 23.97) * mm, "end": v(-160, -16.03) * mm});
            skLineSegment(sketch, "E215.right", {"start": v(-120, 23.97) * mm, "end": v(-120, -16.03) * mm});
            skPoint(sketch, "E215.middle", {"position": v(-140, 3.97) * mm});
            skSolve(sketch);
        }
        {
            var Q0;
            Q0 = qSketchRegion(id + "F67", true);
            extrude(context, id + "F68", {"entities" : qUnion([Q0]), "depth" : 60 * mm});
        }
        {
            var Q0;
            Q0=makeQuery(id+"F68.opExtrude","SWEPT_FACE",FACE,{"disambiguationData":[OSD([sQuery(id+"F67.wireOp",EDGE,"E215.bottom")])]});
            var sketch = newSketch(context, id + "F69", { "sketchPlane" : qUnion([Q0])});
            skLineSegment(sketch, "E216.0", {"start": v(917.5, -35) * mm, "end": v(952.5, -35) * mm, "construction": true});
            skLineSegment(sketch, "E217", {"start": v(935, -120) * mm, "end": v(935, -160) * mm, "construction": true});
            skLineSegment(sketch, "E218.0.0", {"start": v(896, -120) * mm, "end": v(896, -160) * mm, "construction": true});
            skLineSegment(sketch, "E218.0.1", {"start": v(896, -160) * mm, "end": v(956, -160) * mm, "construction": true});
            skLineSegment(sketch, "E218.0.2", {"start": v(956, -160) * mm, "end": v(956, -120) * mm, "construction": true});
            skLineSegment(sketch, "E218.0.3", {"start": v(956, -120) * mm, "end": v(896, -120) * mm, "construction": true});
            skLineSegment(sketch, "E219", {"start": v(956, -140) * mm, "end": v(857.2, -140) * mm, "construction": true});
            skPoint(sketch, "E219.endSnap0", {"position": v(956, -140) * mm});
            skPoint(sketch, "E220.orphan", {"position": v(935, -35) * mm});
            skPoint(sketch, "E221", {"position": v(935, -140) * mm});
            skSolve(sketch);
        }
        {
            var Q0;
            Q0=sQuery(id+"F69.wireOp",VERTEX,"E221");
            var Q1;
            Q1=makeQuery(id+"F68.opExtrude","SWEPT_BODY",BODY,{"disambiguationData":[OSD([sQuery(id+"F67.wireOp",EDGE,"E215.bottom"),sQuery(id+"F67.wireOp",EDGE,"E215.top"),sQuery(id+"F67.wireOp",EDGE,"E215.left"),sQuery(id+"F67.wireOp",EDGE,"E215.right")])]});
            hole(context, id + "F70", {"style" : HoleStyle.SIMPLE, "endStyle" : HoleEndStyle.THROUGH, "standardTappedOrClearance" : lookupTablePath({ "standard" : "ISO", "size" : "20", "type" : "Drilled" }), "standardBlindInLast" : lookupTablePath({ "standard" : "ISO", "size" : "20", "type" : "Drilled" }), "holeDiameter" : 20 * mm, "locations" : qUnion([Q0]), "scope" : qUnion([Q1]), "isTappedThrough" : true});
        }
        {
            var Q0;
            Q0=makeQuery(id+"F68.opExtrude","SWEPT_FACE",FACE,{"disambiguationData":[OSD([sQuery(id+"F67.wireOp",EDGE,"E215.left")])]});
            var sketch = newSketch(context, id + "F71", { "sketchPlane" : qUnion([Q0])});
            skLineSegment(sketch, "E222.0", {"start": v(925, 23.97) * mm, "end": v(945, 23.97) * mm, "construction": true});
            skLineSegment(sketch, "E223", {"start": v(935, 23.97) * mm, "end": v(935, -16.03) * mm, "construction": true});
            skLineSegment(sketch, "E224.0", {"start": v(956, -16.03) * mm, "end": v(896, -16.03) * mm, "construction": true});
            skPoint(sketch, "E225", {"position": v(935, 3.97) * mm});
            skSolve(sketch);
        }
        {
            var Q0;
            Q0=sQuery(id+"F71.wireOp",VERTEX,"E225");
            var Q1;
            Q1=makeQuery(id+"F68.opExtrude","SWEPT_BODY",BODY,{"disambiguationData":[OSD([sQuery(id+"F67.wireOp",EDGE,"E215.bottom"),sQuery(id+"F67.wireOp",EDGE,"E215.top"),sQuery(id+"F67.wireOp",EDGE,"E215.left"),sQuery(id+"F67.wireOp",EDGE,"E215.right")])]});
            hole(context, id + "F72", {"style" : HoleStyle.SIMPLE, "endStyle" : HoleEndStyle.THROUGH, "standardTappedOrClearance" : lookupTablePath({ "standard" : "ISO", "size" : "8", "type" : "Drilled" }), "standardBlindInLast" : lookupTablePath({ "standard" : "ISO", "size" : "8", "type" : "Drilled" }), "holeDiameter" : 8 * mm, "locations" : qUnion([Q0]), "scope" : qUnion([Q1]), "isTappedThrough" : true});
        }
        {
            var Q0;
            Q0=makeQuery(id+"F68.opExtrude","SWEPT_BODY",BODY,{"disambiguationData":[OSD([sQuery(id+"F67.wireOp",EDGE,"E215.bottom"),sQuery(id+"F67.wireOp",EDGE,"E215.top"),sQuery(id+"F67.wireOp",EDGE,"E215.left"),sQuery(id+"F67.wireOp",EDGE,"E215.right")])]});
            var Q1;
            Q1=qCreatedBy(makeId("Right.planeOp"),FACE);
            mirror(context, id + "F73", {"entities" : qUnion([Q0]), "mirrorPlane" : qUnion([Q1])});
        }
        {
            var Q0;
            Q0=makeQuery(id+"F51.opExtrude","SWEPT_BODY",BODY,{"disambiguationData":[OSD([sQuery(id+"F50.wireOp",EDGE,"E175.0.0"),sQuery(id+"F50.wireOp",EDGE,"E175.0.1"),sQuery(id+"F50.wireOp",EDGE,"E175.0.8"),sQuery(id+"F50.wireOp",EDGE,"E176")])]});
            var Q1;
            Q1=qCreatedBy(id+"F55.planeOp",FACE);
            mirror(context, id + "F74", {"entities" : qUnion([Q0]), "mirrorPlane" : qUnion([Q1])});
        }
        {
            var Q0;
            Q0=makeQuery(id+"F51.opExtrude","SWEPT_BODY",BODY,{"disambiguationData":[OSD([sQuery(id+"F50.wireOp",EDGE,"E175.0.0"),sQuery(id+"F50.wireOp",EDGE,"E175.0.1"),sQuery(id+"F50.wireOp",EDGE,"E175.0.8"),sQuery(id+"F50.wireOp",EDGE,"E176")])]});
            var Q1;
            Q1=makeQuery(id+"F74.opPattern","COPY",BODY,{"derivedFrom":makeQuery(id+"F51.opExtrude","SWEPT_BODY",BODY,{"disambiguationData":[OSD([sQuery(id+"F50.wireOp",EDGE,"E175.0.0"),sQuery(id+"F50.wireOp",EDGE,"E175.0.1"),sQuery(id+"F50.wireOp",EDGE,"E175.0.8"),sQuery(id+"F50.wireOp",EDGE,"E176")])]}),"instanceName":"1"});
            var Q2;
            Q2=qCreatedBy(makeId("Right.planeOp"),FACE);
            mirror(context, id + "F75", {"entities" : qUnion([Q0, Q1]), "mirrorPlane" : qUnion([Q2])});
        }
    });
